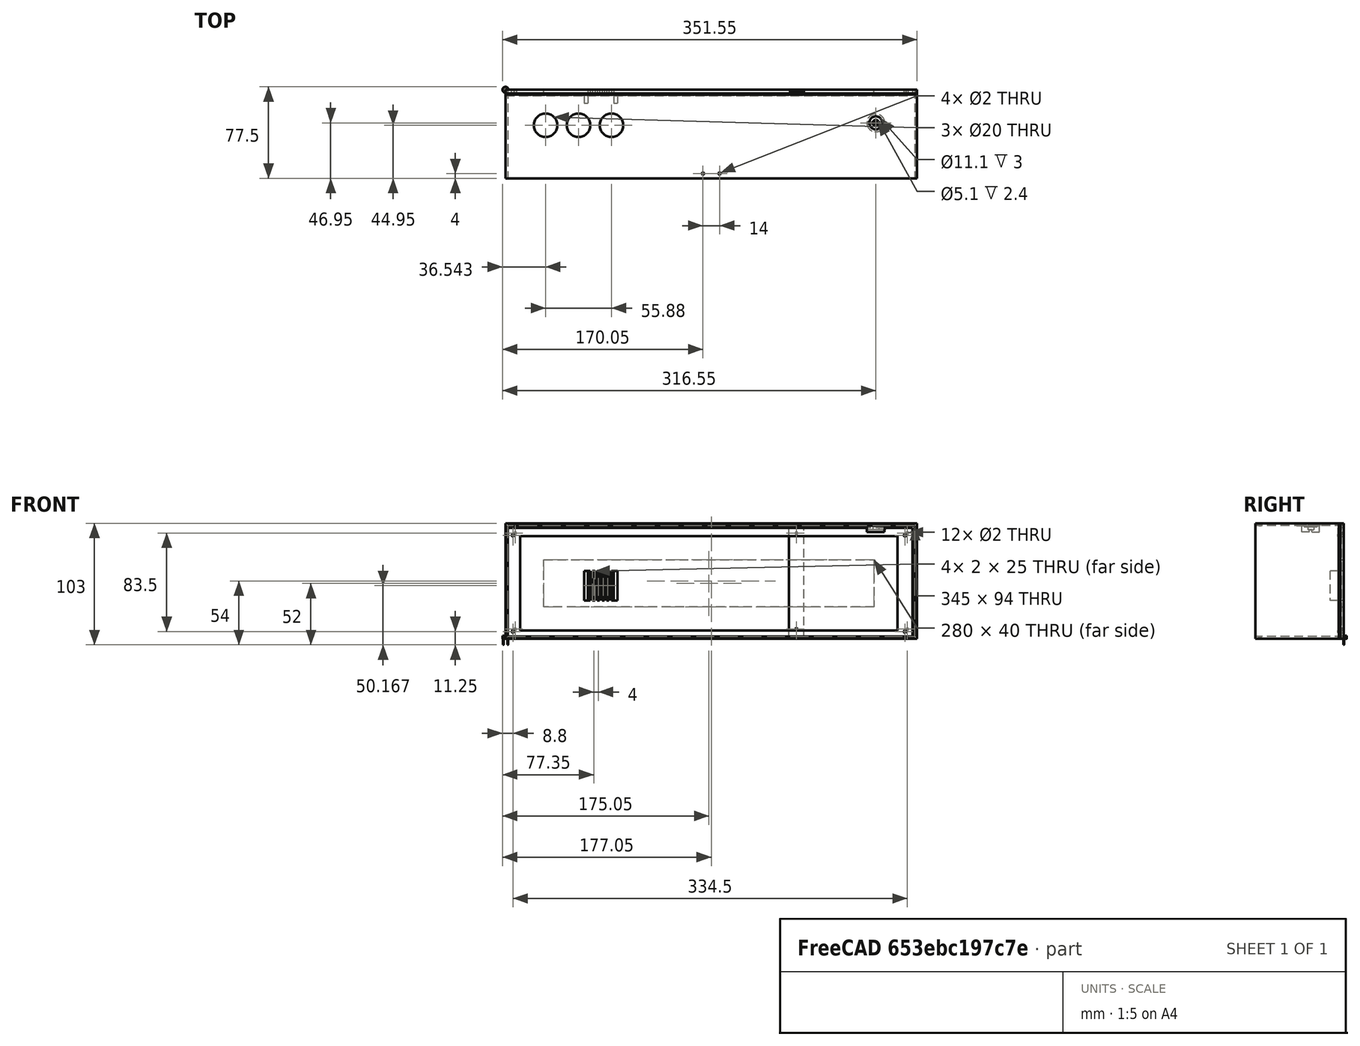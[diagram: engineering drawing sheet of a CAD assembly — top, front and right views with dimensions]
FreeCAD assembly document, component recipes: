
FREECAD ASSEMBLY — COMPONENT RECIPES ("display")

This assembly document has 32 components, labeled P0..P31 below (a component is one placed body or linked part). 31 of them carry a construction recipe — the FreeCAD feature program that regenerates the part from scratch, quoted from this document or its linked companion documents; the rest are supplied as boundary geometry only. No exploded tour is included for this assembly.
COMPONENT P0 — recipe-attached ("BackPlateBody001", modeled in this document).
Construction recipe (the document's own serialized feature program — sketch geometry with constraints, then the solid features built on it; lengths are millimeters unless a unit is written):

FEATURE [Sketcher::SketchObject] Sketch022
  ArcFitTolerance = 1e-06
  AttachmentSupport = -> [XZ_Plane007]
  FullyConstrained = true
  MakeInternals = false
  MapMode = 5
  Placement = pos=(0,0,0) rot=(1,0,0;1.5708rad)
  expr: Constraints[10] = <<CalculatedSS>>.back_plate_width
  expr: Constraints[91] = <<CalculatedSS>>.dht_vertical_offset
  expr: Constraints[92] = <<CalculatedSS>>.dht_horizontal_offset
  expr: Constraints[93] = <<DisplaySS>>.case_thickness + mount_bracket#<<DisplaySS>>.mount_bracket_face_size / 2
  expr: Constraints[94] = <<CalculatedSS>>.split_offset - <<CalculatedSS>>.mount_bracket_face_size / 2
  expr: Constraints[95] = <<DisplaySS>>.screw_diameter
  expr: Constraints[96] = <<CalculatedSS>>.split_offset - <<CalculatedSS>>.mount_bracket_face_size / 2
  expr: Constraints[97] = <<CalculatedSS>>.case_height - <<DisplaySS>>.case_thickness - <<mount_bracket>>#<<DisplaySS>>.mount_bracket_face_size / 2
  expr: Constraints[98] = <<DisplaySS>>.screw_diameter
  expr: Constraints[9] = <<CalculatedSS>>.back_plate_height
  sketch-geometry (35):
    g0: LineSegment StartX=0 StartY=98 StartZ=0 EndX=0 EndY=0 EndZ=0
    g1: LineSegment StartX=0 StartY=0 StartZ=0 EndX=349 EndY=0 EndZ=0
    g2: LineSegment StartX=349 StartY=0 StartZ=0 EndX=349 EndY=98 EndZ=0
    g3: LineSegment StartX=349 StartY=98 StartZ=0 EndX=0 EndY=98 EndZ=0
    g4: LineSegment StartX=69.8 StartY=57.6667 StartZ=0 EndX=69.8 EndY=32.6667 EndZ=0
    g5: LineSegment StartX=69.8 StartY=32.6667 StartZ=0 EndX=71.8 EndY=32.6667 EndZ=0
    g6: LineSegment StartX=71.8 StartY=32.6667 StartZ=0 EndX=71.8 EndY=57.6667 EndZ=0
    g7: LineSegment StartX=71.8 StartY=57.6667 StartZ=0 EndX=69.8 EndY=57.6667 EndZ=0
    g8: LineSegment StartX=73.8 StartY=57.6667 StartZ=0 EndX=73.8 EndY=32.6667 EndZ=0
    g9: LineSegment StartX=73.8 StartY=32.6667 StartZ=0 EndX=75.8 EndY=32.6667 EndZ=0
    g10: LineSegment StartX=75.8 StartY=32.6667 StartZ=0 EndX=75.8 EndY=57.6667 EndZ=0
    g11: LineSegment StartX=75.8 StartY=57.6667 StartZ=0 EndX=73.8 EndY=57.6667 EndZ=0
    g12: LineSegment StartX=77.8 StartY=57.6667 StartZ=0 EndX=77.8 EndY=32.6667 EndZ=0
    g13: LineSegment StartX=77.8 StartY=32.6667 StartZ=0 EndX=79.8 EndY=32.6667 EndZ=0
    g14: LineSegment StartX=79.8 StartY=32.6667 StartZ=0 EndX=79.8 EndY=57.6667 EndZ=0
    g15: LineSegment StartX=79.8 StartY=57.6667 StartZ=0 EndX=77.8 EndY=57.6667 EndZ=0
    g16: LineSegment StartX=81.8 StartY=57.6667 StartZ=0 EndX=81.8 EndY=32.6667 EndZ=0
    g17: LineSegment StartX=81.8 StartY=32.6667 StartZ=0 EndX=83.8 EndY=32.6667 EndZ=0
    g18: LineSegment StartX=83.8 StartY=32.6667 StartZ=0 EndX=83.8 EndY=57.6667 EndZ=0
    g19: LineSegment StartX=83.8 StartY=57.6667 StartZ=0 EndX=81.8 EndY=57.6667 EndZ=0
    g20: LineSegment StartX=85.8 StartY=57.6667 StartZ=0 EndX=85.8 EndY=32.6667 EndZ=0
    g21: LineSegment StartX=85.8 StartY=32.6667 StartZ=0 EndX=87.8 EndY=32.6667 EndZ=0
    g22: LineSegment StartX=87.8 StartY=32.6667 StartZ=0 EndX=87.8 EndY=57.6667 EndZ=0
    g23: LineSegment StartX=87.8 StartY=57.6667 StartZ=0 EndX=85.8 EndY=57.6667 EndZ=0
    g24: LineSegment StartX=89.8 StartY=57.6667 StartZ=0 EndX=89.8 EndY=32.6667 EndZ=0
    g25: LineSegment StartX=89.8 StartY=32.6667 StartZ=0 EndX=91.8 EndY=32.6667 EndZ=0
    g26: LineSegment StartX=91.8 StartY=32.6667 StartZ=0 EndX=91.8 EndY=57.6667 EndZ=0
    g27: LineSegment StartX=91.8 StartY=57.6667 StartZ=0 EndX=89.8 EndY=57.6667 EndZ=0
    g28: LineSegment [constr] StartX=71.8 StartY=57.6667 StartZ=0 EndX=73.8 EndY=57.6667 EndZ=0
    g29: LineSegment [constr] StartX=75.8 StartY=57.6667 StartZ=0 EndX=77.8 EndY=57.6667 EndZ=0
    g30: LineSegment [constr] StartX=79.8 StartY=57.6667 StartZ=0 EndX=81.8 EndY=57.6667 EndZ=0
    g31: LineSegment [constr] StartX=83.8 StartY=57.6667 StartZ=0 EndX=85.8 EndY=57.6667 EndZ=0
    g32: LineSegment [constr] StartX=87.8 StartY=57.6667 StartZ=0 EndX=89.8 EndY=57.6667 EndZ=0
    g33: Circle CenterX=246.75 CenterY=8.25 CenterZ=0 NormalX=0 NormalY=0 NormalZ=1 AngleXU=0 Radius=1
    g34: Circle CenterX=246.75 CenterY=89.75 CenterZ=0 NormalX=0 NormalY=0 NormalZ=1 AngleXU=0 Radius=1
  constraints (99):
    c: Coincident(g0,g1)
    c: Coincident(g1,g2)
    c: Coincident(g2,g3)
    c: Coincident(g3,g0)
    c: Vertical(g0)
    c: Vertical(g2)
    c: Horizontal(g1)
    c: Horizontal(g3)
    c: Coincident(g0,g-1)
    c: Distance(g0) = 98
    c: Distance(g1) = 349
    c: Coincident(g4,g5)
    c: Coincident(g5,g6)
    c: Coincident(g6,g7)
    c: Coincident(g7,g4)
    c: Vertical(g4)
    c: Vertical(g6)
    c: Horizontal(g5)
    c: Horizontal(g7)
    c: Distance(g6) = 25
    c: Distance(g7) = 2
    c: Coincident(g8,g9)
    c: Coincident(g12,g13)
    c: Coincident(g16,g17)
    c: Coincident(g20,g21)
    c: Coincident(g24,g25)
    c: Coincident(g9,g10)
    c: Coincident(g13,g14)
    c: Coincident(g17,g18)
    c: Coincident(g21,g22)
    c: Coincident(g25,g26)
    c: Coincident(g10,g11)
    c: Coincident(g14,g15)
    c: Coincident(g18,g19)
    c: Coincident(g22,g23)
    c: Coincident(g26,g27)
    c: Coincident(g11,g8)
    c: Coincident(g15,g12)
    c: Coincident(g19,g16)
    c: Coincident(g23,g20)
    c: Coincident(g27,g24)
    c: Vertical(g8)
    c: Vertical(g12)
    c: Vertical(g16)
    c: Vertical(g20)
    c: Vertical(g24)
    c: Vertical(g10)
    c: Vertical(g14)
    c: Vertical(g18)
    c: Vertical(g22)
    c: Vertical(g26)
    c: Horizontal(g9)
    c: Horizontal(g13)
    c: Horizontal(g17)
    c: Horizontal(g21)
    c: Horizontal(g25)
    c: Horizontal(g11)
    c: Horizontal(g15)
    c: Horizontal(g19)
    c: Horizontal(g23)
    c: Horizontal(g27)
    c: Coincident(g28,g6)
    c: Coincident(g28,g8)
    c: Horizontal(g28)
    c: Coincident(g29,g10)
    c: Coincident(g29,g12)
    c: Horizontal(g29)
    c: Coincident(g30,g14)
    c: Coincident(g30,g16)
    c: Horizontal(g30)
    c: Coincident(g31,g18)
    c: Coincident(g31,g20)
    c: Horizontal(g31)
    c: Coincident(g32,g22)
    c: Coincident(g32,g24)
    c: Horizontal(g32)
    c: DistanceX(g6,g8) = 2
    c: Equal(g11,g7)
    c: Equal(g7,g15)
    c: Equal(g15,g19)
    c: Equal(g19,g23)
    c: Equal(g23,g27)
    c: Equal(g29,g28)
    c: Equal(g28,g30)
    c: Equal(g30,g31)
    c: Equal(g31,g32)
    c: Horizontal(g4,g8)
    c: Horizontal(g8,g12)
    c: Horizontal(g12,g16)
    c: Horizontal(g16,g20)
    c: Horizontal(g20,g24)
    c: DistanceY(g-1,g4) = 32.6667
    c: DistanceX(g-1,g4) = 69.8
    c: DistanceY(g-1,g33) = 8.25
    c: DistanceX(g-2,g33) = 246.75
    c: Diameter(g33) = 2
    c: DistanceX(g-2,g34) = 246.75
    c: DistanceY(g-1,g34) = 89.75
    c: Diameter(g34) = 2
FEATURE [PartDesign::Pad] Pad007  label="BackPlatePad"
  Direction = (0,-1,2e-16)
  Length = 4
  Length2 = 10
  Placement = pos=(0,0,0) rot=(1,0,0;1.5708rad)
  Profile = -> Sketch022
  ReferenceAxis = -> Sketch022 [N_Axis]
  Refine = true
  Suppressed = false
  Type = 0
  expr: Length = <<DisplaySS>>.back_plate_thickness
FEATURE [Sketcher::SketchObject] Sketch023
  ArcFitTolerance = 1e-06
  AttachmentSupport = -> [XZ_Plane007]
  FullyConstrained = true
  MakeInternals = false
  MapMode = 5
  Placement = pos=(0,0,0) rot=(1,0,0;1.5708rad)
  expr: Constraints[0] = <<CalculatedSS>>.backplate_screw_offset_x
  expr: Constraints[1] = <<CalculatedSS>>.backplate_screw_offset_y
  expr: Constraints[2] = <<DisplaySS>>.screw_diameter
  sketch-geometry (1):
    g0: Circle CenterX=8.25 CenterY=8.25 CenterZ=0 NormalX=0 NormalY=0 NormalZ=1 AngleXU=0 Radius=1
  constraints (3):
    c: DistanceX(g-2,g0) = 8.25
    c: DistanceY(g-1,g0) = 8.25
    c: Diameter(g0) = 2
FEATURE [PartDesign::Plane] DatumPlane012
  AttachmentOffset = pos=(0,0,174.5) rot=(0,0,1;0rad)
  AttachmentSupport = -> [Pad007]
  Length = 138.684
  MapMode = 4
  Placement = pos=(174.5,0,-3.87e-14) rot=(0.707107,0,0.707107;3.14159rad)
  ResizeMode = 0
  Width = 65.6844
  expr: .AttachmentOffset.Base.z = <<CalculatedSS>>.back_plate_width / 2
FEATURE [PartDesign::Plane] DatumPlane013
  AttachmentOffset = pos=(0,0,-49) rot=(0,0,1;0rad)
  AttachmentSupport = -> [Pad007]
  Length = 401.35
  MapMode = 3
  Placement = pos=(0,0,49) rot=(1,0,0;3.14159rad)
  ResizeMode = 0
  Width = 77.3496
  expr: .AttachmentOffset.Base.z = <<CalculatedSS>>.back_plate_height / 2 * -1
FEATURE [Sketcher::SketchObject] Sketch026
  ArcFitTolerance = 1e-06
  AttachmentSupport = -> [XZ_Plane007]
  ExternalGeometry = -> [Sketch022]
  FullyConstrained = true
  MakeInternals = false
  MapMode = 5
  Placement = pos=(0,0,0) rot=(1,0,0;1.5708rad)
  sketch-geometry (8):
    g0: LineSegment StartX=69.8 StartY=57.6667 StartZ=0 EndX=66.8 EndY=57.6667 EndZ=0
    g1: LineSegment StartX=66.8 StartY=57.6667 StartZ=0 EndX=66.8 EndY=32.6667 EndZ=0
    g2: LineSegment StartX=66.8 StartY=32.6667 StartZ=0 EndX=69.8 EndY=32.6667 EndZ=0
    g3: LineSegment StartX=69.8 StartY=32.6667 StartZ=0 EndX=69.8 EndY=57.6667 EndZ=0
    g4: LineSegment StartX=91.8 StartY=57.6667 StartZ=0 EndX=91.8 EndY=32.6667 EndZ=0
    g5: LineSegment StartX=91.8 StartY=32.6667 StartZ=0 EndX=94.8 EndY=32.6667 EndZ=0
    g6: LineSegment StartX=94.8 StartY=32.6667 StartZ=0 EndX=94.8 EndY=57.6667 EndZ=0
    g7: LineSegment StartX=94.8 StartY=57.6667 StartZ=0 EndX=91.8 EndY=57.6667 EndZ=0
  constraints (20):
    c: Coincident(g0,g1)
    c: Coincident(g1,g2)
    c: Coincident(g2,g3)
    c: Coincident(g3,g0)
    c: Horizontal(g0)
    c: Horizontal(g2)
    c: Vertical(g1)
    c: Coincident(g0,g-6)
    c: Coincident(g4,g5)
    c: Coincident(g5,g6)
    c: Coincident(g6,g7)
    c: Coincident(g7,g4)
    c: Vertical(g6)
    c: Horizontal(g5)
    c: Horizontal(g7)
    c: Coincident(g4,g-3)
    c: Coincident(g4,g-4)
    c: Coincident(g2,g-5)
    c: Distance(g2) = 3
    c: Equal(g2,g5)
FEATURE [PartDesign::Pad] Pad008
  BaseFeature = -> Pad007
  Direction = (0,-1,2e-16)
  Length = 11.7
  Length2 = 10
  Placement = pos=(0,0,0) rot=(1,0,0;1.5708rad)
  Profile = -> Sketch026
  ReferenceAxis = -> Sketch026 [N_Axis]
  Refine = true
  Suppressed = false
  Type = 0
  expr: Length = <<DisplaySS>>.back_plate_thickness + <<DisplaySS>>.dht_depth
FEATURE [PartDesign::Plane] DatumPlane015  label="BackPlateFace"
  AttachmentOffset = pos=(0,0,4) rot=(0,0,1;0rad)
  AttachmentSupport = -> [Pad008]
  Length = 416.896
  MapMode = 2
  Placement = pos=(0,-4,9e-16) rot=(1,0,0;1.5708rad)
  ResizeMode = 0
  Width = 165.896
  expr: .AttachmentOffset.Base.z = <<DisplaySS>>.back_plate_thickness
FEATURE [Sketcher::SketchObject] Sketch027  label="MountStudSketch"
  ArcFitTolerance = 1e-06
  AttachmentSupport = -> [DatumPlane015]
  ExternalGeometry = -> [Sketch026]
  FullyConstrained = true
  MakeInternals = false
  MapMode = 5
  Placement = pos=(0,-4,9e-16) rot=(1,0,0;1.5708rad)
  expr: Constraints[0] = <<mount_stud>>#<<MountStudSS>>.base_diameter
  expr: Constraints[6] = mount_stud#<<MountStudSS>>.base_diameter / 2
  sketch-geometry (4):
    g0: Circle CenterX=80.8 CenterY=23.3932 CenterZ=0 NormalX=0 NormalY=0 NormalZ=1 AngleXU=0 Radius=9.2735
    g1: LineSegment [constr] StartX=80.8 StartY=23.3932 StartZ=0 EndX=66.8 EndY=32.6667 EndZ=0
    g2: LineSegment [constr] StartX=80.8 StartY=23.3932 StartZ=0 EndX=94.8 EndY=32.6667 EndZ=0
    g3: LineSegment StartX=80.8 StartY=23.3932 StartZ=0 EndX=80.8 EndY=32.6667 EndZ=0
  constraints (10):
    c: Diameter(g0) = 18.547
    c: Coincident(g1,g0)
    c: Coincident(g1,g-3)
    c: Coincident(g2,g0)
    c: Coincident(g2,g-4)
    c: Equal(g2,g1)
    c: DistanceY(g0,g1) = 9.2735
    c: Coincident(g3,g0)
    c: PointOnObject(g3,g0)
    c: Vertical(g3)
FEATURE [PartDesign::Mirrored] Mirrored
  MirrorPlane = -> DatumPlane013
  Placement = pos=(0,0,0) rot=(1,0,0;1.5708rad)
  Refine = true
  Suppressed = false
  TransformMode = 0
FEATURE [PartDesign::Mirrored] Mirrored006
  MirrorPlane = -> DatumPlane012
  Placement = pos=(0,0,0) rot=(1,0,0;1.5708rad)
  Refine = true
  Suppressed = false
  TransformMode = 0
FEATURE [PartDesign::Pocket] Pocket014
  BaseFeature = -> Pad008
  Direction = (0,1,-2e-16)
  Length = 4
  Length2 = 5
  Placement = pos=(0,0,0) rot=(1,0,0;1.5708rad)
  Profile = -> Sketch023
  ReferenceAxis = -> Sketch023 [N_Axis]
  Refine = true
  Reversed = true
  Suppressed = false
  Type = 0
  expr: Length = <<DisplaySS>>.back_plate_thickness
FEATURE [PartDesign::MultiTransform] MultiTransform
  BaseFeature = -> Pocket014
  Originals = -> [Pocket014]
  Placement = pos=(0,0,0) rot=(1,0,0;1.5708rad)
  Refine = true
  Suppressed = false
  TransformMode = 0
  Transformations = -> [Mirrored,Mirrored006]
FEATURE [PartDesign::Plane] DatumPlane017
  AttachmentOffset = pos=(0,0,2) rot=(0,0,1;0rad)
  AttachmentSupport = -> [XY_Plane007]
  Length = 416.896
  MapMode = 3
  Placement = pos=(0,-2,4e-16) rot=(1,0,0;1.5708rad)
  ResizeMode = 0
  Width = 165.896
  expr: .AttachmentOffset.Base.z = <<DisplaySS>>.back_plate_thickness / 2
FEATURE [Sketcher::SketchObject] Sketch039  label="CutSketch"
  ArcFitTolerance = 1e-06
  AttachmentSupport = -> [XY_Plane007]
  FullyConstrained = true
  MakeInternals = false
  MapMode = 5
  expr: Constraints[19] = <<DisplaySS>>.back_plate_thickness / 2
  expr: Constraints[20] = <<CalculatedSS>>.mount_bracket_face_size
  expr: Constraints[30] = <<DisplaySS>>.back_plate_thickness / 2
  expr: Constraints[41] = <<CalculatedSS>>.split_offset
  expr: Constraints[42] = <<CalculatedSS>>.case_width
  expr: Constraints[9] = <<DisplaySS>>.back_plate_thickness + <<DisplaySS>>.dht_depth
  sketch-geometry (16):
    g0: LineSegment StartX=0 StartY=0 StartZ=0 EndX=0 EndY=-11.7 EndZ=0
    g1: LineSegment StartX=0 StartY=-11.7 StartZ=0 EndX=240.5 EndY=-11.7 EndZ=0
    g2: LineSegment StartX=240.5 StartY=-11.7 StartZ=0 EndX=240.5 EndY=0 EndZ=0
    g3: LineSegment StartX=240.5 StartY=0 StartZ=0 EndX=0 EndY=0 EndZ=0
    g4: LineSegment StartX=240.5 StartY=0 StartZ=0 EndX=240.5 EndY=-2 EndZ=0
    g5: LineSegment StartX=240.5 StartY=-2 StartZ=0 EndX=253 EndY=-2 EndZ=0
    g6: LineSegment StartX=253 StartY=-2 StartZ=0 EndX=253 EndY=0 EndZ=0
    g7: LineSegment StartX=253 StartY=0 StartZ=0 EndX=240.5 EndY=0 EndZ=0
    g8: LineSegment StartX=240.5 StartY=-2 StartZ=0 EndX=240.5 EndY=-4 EndZ=0
    g9: LineSegment StartX=240.5 StartY=-4 StartZ=0 EndX=253 EndY=-4 EndZ=0
    g10: LineSegment StartX=253 StartY=-4 StartZ=0 EndX=253 EndY=-2 EndZ=0
    g11: LineSegment StartX=253 StartY=-2 StartZ=0 EndX=240.5 EndY=-2 EndZ=0
    g12: LineSegment StartX=253 StartY=-4 StartZ=0 EndX=349 EndY=-4 EndZ=0
    g13: LineSegment StartX=349 StartY=-4 StartZ=0 EndX=349 EndY=0 EndZ=0
    g14: LineSegment StartX=349 StartY=0 StartZ=0 EndX=253 EndY=0 EndZ=0
    g15: LineSegment StartX=253 StartY=0 StartZ=0 EndX=253 EndY=-4 EndZ=0
  constraints (43):
    c: Coincident(g0,g1)
    c: Coincident(g1,g2)
    c: Coincident(g2,g3)
    c: Coincident(g3,g0)
    c: Vertical(g0)
    c: Vertical(g2)
    c: Horizontal(g1)
    c: Horizontal(g3)
    c: Coincident(g0,g-1)
    c: Distance(g0) = 11.7
    c: Coincident(g4,g5)
    c: Coincident(g5,g6)
    c: Coincident(g6,g7)
    c: Coincident(g7,g4)
    c: Vertical(g4)
    c: Vertical(g6)
    c: Horizontal(g5)
    c: Horizontal(g7)
    c: Coincident(g4,g2)
    c: Distance(g6) = 2
    c: Distance(g5) = 12.5
    c: Coincident(g8,g9)
    c: Coincident(g9,g10)
    c: Coincident(g10,g11)
    c: Coincident(g11,g8)
    c: Vertical(g8)
    c: Vertical(g10)
    c: Horizontal(g9)
    c: Coincident(g8,g4)
    c: Coincident(g10,g5)
    c: Distance(g10) = 2
    c: Coincident(g12,g13)
    c: Coincident(g13,g14)
    c: Coincident(g14,g15)
    c: Coincident(g15,g12)
    c: Horizontal(g12)
    c: Horizontal(g14)
    c: Vertical(g13)
    c: Vertical(g15)
    c: Coincident(g12,g9)
    c: PointOnObject(g13,g-1)
    c: DistanceX(g-1,g6) = 253
    c: DistanceX(g-2,g13) = 349
FEATURE [PartDesign::Body] Body006  label="FullBackPlateBody"
  AllowCompound = false
  Group = -> [Sketch022,Pad007,Sketch023,DatumPlane012,DatumPlane013,Mirrored,Mirrored006,Sketch026,Pad008,DatumPlane015,Sketch027,Pocket014,MultiTransform,DatumPlane017,Sketch039]
  Origin = -> Origin007
  Tip = -> MultiTransform
COMPONENT P1 — same part as P0; its construction recipe is shown at P0.
COMPONENT P2 — same part as P0; its construction recipe is shown at P0.
COMPONENT P3 — same part as P0; its construction recipe is shown at P0.
COMPONENT P4 — recipe-attached ("Grid", a linked part whose construction recipe lives in a companion FreeCAD document of the same project; that document's serialized recipe follows).
Construction recipe (the companion document, serialized — sketch geometry with constraints, then the solid features built on it; lengths are millimeters unless a unit is written):

FCSTD DOCUMENT  (FreeCAD 1.0R39109 (Git))
Label: grid
License: All rights reserved
LicenseURL: https://en.wikipedia.org/wiki/All_rights_reserved
objects: Sketcher::SketchObject×7, PartDesign::Mirrored×6, PartDesign::Pocket×6, PartDesign::Plane×4, PartDesign::MultiTransform×4, Spreadsheet::Sheet×2, PartDesign::LinearPattern×2, PartDesign::Pad×1, PartDesign::Body×1
note: 64 computed .brp shape members not serialized (recipe doc carries the construction recipe); baked Part::Feature solids carry a one-line shape summary decoded from their .brp

FEATURE [Spreadsheet::Sheet] Spreadsheet  label="GridDisplaySS"
  Body = 0
  cells = A1='Variant; B1='case_depth; C1='matrix_height; D1='matrix_width; E1='matrix_depth; F1='threaded_insert_depth; G1='threaded_insert_outer_diameter; H1='threaded_insert_safety_zone; I1='case_thickness; J1='grid_border_thickness; K1='grid_depth; L1='grid_intercell_spacing; M1='grid_cell_width; N1='led_x_count; O1='led_y_count; P1='grid_countersink_hole_depth; Q1='magnet_diameter; R1='magnet_height; S1='printer_tolerance_modifier; T1='screw_diameter; U1='mount_panel_exclusion_offset; V1='glass_thickness; W1='top_component_offset; X1='photoresistor_diameter; Y1='photoresistor_truncated_width; Z1='photoresistor_height; AA1='top_component_horizontal_offset; AB1='top_component_spacing; AC1='photoresistor_ledge_size; AD1='back_plate_thickness; A2==hiddenref(.Body.String); B2(case_depth)==.B3; C2(matrix_height)==.C3; D2(matrix_width)==.D3; E2(matrix_depth)==.E3; F2(threaded_insert_depth)==.F3; G2(threaded_insert_outer_diameter)==.G3; H2(threaded_insert_safety_zone)==.H3; I2(case_thickness)==.I3; J2(grid_border_thickness)==.J3; K2(grid_depth)==.K3; L2(grid_intercell_spacing)==.L3; M2(grid_cell_width)==.M3; N2(led_x_count)==.N3; O2(led_y_count)==.O3; P2(grid_countersink_hole_depth)==.P3; Q2(magnet_diameter)==.Q3; R2(magnet_height)==.R3; S2(printer_tolerance_modifier)==.S3; T2(screw_diameter)==.T3; U2(mount_panel_exclusion_offset)==.U3; V2(glass_thickness)==.V3; W2(top_component_offset)==.W3; X2(photoresistor_diameter)==.X3; Y2(photoresistor_truncated_width)==.Y3; Z2(photoresistor_height)==.Z3; AA2(top_component_horizontal_offset)==.AA3; AB2(top_component_spacing)==.AB3; AC2(photoresistor_ledge_size)==.AC3; AD2(back_plate_thickness)==.AD3; A3='A; B3==6 cm; C3==80 mm; D3==320 mm; E3==2 mm; F3==4 mm; G3==5 mm; H3==2 mm; I3==2 mm; J3==3 mm; K3==8 mm; L3==1 mm; M3==9 mm; N3=32; O3=8; P3==3 mm; Q3==5 mm; R3==2.8 mm; S3==1 mm; T3==2 mm; U3==2 cm; V3==3 mm; W3==2 cm; X3==5.1 mm; Y3==4.5 mm; Z3==2.4 mm; AA3==2 cm; AB3==0.5 cm; AC3==3 mm; AD3==4 mm
  expr: .Body.Enum = cells[<<A3:|>>]
  expr: .cells.Bind.B2.ZZ2 = tuple(.cells; <<B>> + str(hiddenref(Body) + 3); <<ZZ>> + str(hiddenref(Body) + 3))
FEATURE [Spreadsheet::Sheet] Spreadsheet001  label="GridCalculatedSS"
  cells = B1='grid_horizontal_padding; C1='grid_vertical_padding; D1='case_height; E1='case_width; F1='grid_width; G1='grid_height; H1='grid_matrix_width; I1='grid_matrix_height; J1='screw_horizontal_offset; K1='screw_vertical_offset; L1='grid_magnet_vertical_offset; M1='grid_magnet_horizontal_offset; N1='grid_magnet_depth; O1='case_clear_opening_height; P1='case_clear_opening_width; Q1='mounting_plate_thickness; R1='mount_bracket_face_size; S1='case_relative_magnet_horizontal_offset; T1='case_relative_magnet_vertical_offset; U1='split_offset; V1='screw_offset; W1='screw_diameter; X1='screw_depth; B2(grid_horizontal_padding)==<<GridDisplaySS>>.threaded_insert_outer_diameter + <<GridDisplaySS>>.threaded_insert_safety_zone * 2 + <<GridDisplaySS>>.grid_border_thickness + <<GridDisplaySS>>.grid_intercell_spacing / 2; C2(grid_vertical_padding)==screw_depth + 2 mm; D2(case_height)==grid_height + <<GridDisplaySS>>.case_thickness * 2; E2(case_width)==grid_width + <<GridDisplaySS>>.case_thickness * 2; F2(grid_width)==grid_horizontal_padding * 2 + <<GridDisplaySS>>.matrix_width; G2(grid_height)==grid_vertical_padding * 2 + <<GridDisplaySS>>.matrix_height; H2(grid_matrix_width)==grid_width - 2 * grid_horizontal_padding - 10 mm; I2(grid_matrix_height)=70; J2(screw_horizontal_offset)==grid_horizontal_padding / 2; K2(screw_vertical_offset)==mount_bracket_face_size / 2; L2(grid_magnet_vertical_offset)==grid_height / 5; M2(grid_magnet_horizontal_offset)==grid_horizontal_padding / 2; N2(grid_magnet_depth)==<<GridDisplaySS>>.magnet_height * 2; O2(case_clear_opening_height)==grid_height; P2(case_clear_opening_width)==grid_width; Q2(mounting_plate_thickness)==<<GridDisplaySS>>.matrix_depth + 3 mm; R2(mount_bracket_face_size)==screw_horizontal_offset * 2; S2(case_relative_magnet_horizontal_offset)==grid_magnet_horizontal_offset + <<GridDisplaySS>>.case_thickness; T2(case_relative_magnet_vertical_offset)==grid_magnet_vertical_offset + <<GridDisplaySS>>.case_thickness; U2(split_offset)==grid_width / 2; V2(screw_offset)==screw_diameter + 3 mm; W2(screw_diameter)==4 mm; X2(screw_depth)==5 mm
FEATURE [PartDesign::Plane] DatumPlane003  label="Horizontal Dividing Plane"
  AttachmentOffset = pos=(0,0,-47) rot=(0,0,1;0rad)
  AttachmentSupport = -> [XZ_Plane001]
  Length = 397.203
  MapMode = 3
  Placement = pos=(0,0,47) rot=(1,0,0;3.14159rad)
  ResizeMode = 0
  Width = 77.2029
  expr: .AttachmentOffset.Base.z = <<GridCalculatedSS>>.grid_height / 2 * -1
FEATURE [PartDesign::Mirrored] Mirrored006
  MirrorPlane = -> DatumPlane003
  Placement = pos=(0,0,0) rot=(1,0,0;1.5708rad)
  Refine = true
  Suppressed = false
  TransformMode = 0
FEATURE [PartDesign::Plane] DatumPlane002  label="Vertical Dividing Plane"
  AttachmentOffset = pos=(0,0,172.5) rot=(0,0,1;0rad)
  AttachmentSupport = -> [XZ_Plane001]
  Length = 134.427
  MapMode = 4
  Placement = pos=(172.5,0,-3.83e-14) rot=(0.707107,0,0.707107;3.14159rad)
  ResizeMode = 0
  Width = 65.4272
  expr: .AttachmentOffset.Base.z = <<GridCalculatedSS>>.grid_width / 2
FEATURE [PartDesign::Mirrored] Mirrored007
  MirrorPlane = -> DatumPlane002
  Placement = pos=(0,0,0) rot=(1,0,0;1.5708rad)
  Refine = true
  Suppressed = false
  TransformMode = 0
FEATURE [PartDesign::Plane] DatumPlane001  label="Grid Face Plane"
  AttachmentOffset = pos=(0,0,8) rot=(0,0,1;0rad)
  AttachmentSupport = -> [XZ_Plane001]
  Length = 411.967
  MapMode = 2
  Placement = pos=(0,-8,1.8e-15) rot=(1,0,0;1.5708rad)
  ResizeMode = 0
  Width = 160.967
  expr: .AttachmentOffset.Base.z = <<GridDisplaySS>>.grid_depth
FEATURE [Sketcher::SketchObject] Sketch017  label="ScrewHole"
  ArcFitTolerance = 1e-06
  AttachmentSupport = -> [DatumPlane001]
  FullyConstrained = true
  MakeInternals = false
  MapMode = 5
  Placement = pos=(0,-8,1.8e-15) rot=(1,0,0;1.5708rad)
  expr: Constraints[0] = <<GridDisplaySS>>.screw_diameter
  expr: Constraints[1] = <<GridCalculatedSS>>.screw_horizontal_offset
  expr: Constraints[2] = <<GridCalculatedSS>>.screw_vertical_offset
  sketch-geometry (1):
    g0: Circle CenterX=6.25 CenterY=6.25 CenterZ=0 NormalX=0 NormalY=0 NormalZ=1 AngleXU=0 Radius=1
  constraints (3):
    c: Diameter(g0) = 2
    c: DistanceX(g-2,g0) = 6.25
    c: DistanceY(g-1,g0) = 6.25
FEATURE [PartDesign::Mirrored] Mirrored002
  MirrorPlane = -> DatumPlane003
  Placement = pos=(0,0,0) rot=(1,0,0;1.5708rad)
  Refine = true
  Suppressed = false
  TransformMode = 0
FEATURE [PartDesign::Mirrored] Mirrored003
  MirrorPlane = -> DatumPlane002
  Placement = pos=(0,0,0) rot=(1,0,0;1.5708rad)
  Refine = true
  Suppressed = false
  TransformMode = 0
FEATURE [Sketcher::SketchObject] Sketch005  label="Magnet Hole"
  ArcFitTolerance = 1e-06
  AttachmentSupport = -> [DatumPlane001]
  FullyConstrained = true
  MakeInternals = false
  MapMode = 5
  Placement = pos=(0,-8,1.8e-15) rot=(1,0,0;1.5708rad)
  expr: Constraints[0] = <<GridCalculatedSS>>.grid_magnet_horizontal_offset
  expr: Constraints[1] = <<GridCalculatedSS>>.grid_magnet_vertical_offset
  expr: Constraints[2] = <<GridDisplaySS>>.magnet_diameter
  sketch-geometry (1):
    g0: Circle CenterX=6.25 CenterY=18.8 CenterZ=0 NormalX=0 NormalY=0 NormalZ=1 AngleXU=0 Radius=2.5
  constraints (3):
    c: DistanceX(g-2,g0) = 6.25
    c: DistanceY(g-1,g0) = 18.8
    c: Diameter(g0) = 5
FEATURE [PartDesign::Mirrored] Mirrored
  MirrorPlane = -> DatumPlane003
  Placement = pos=(0,0,0) rot=(1,0,0;1.5708rad)
  Refine = true
  Suppressed = false
  TransformMode = 0
FEATURE [PartDesign::Mirrored] Mirrored001
  MirrorPlane = -> DatumPlane002
  Placement = pos=(0,0,0) rot=(1,0,0;1.5708rad)
  Refine = true
  Suppressed = false
  TransformMode = 0
FEATURE [Sketcher::SketchObject] Sketch004
  ArcFitTolerance = 1e-06
  AttachmentSupport = -> [DatumPlane001]
  FullyConstrained = true
  MakeInternals = false
  MapMode = 5
  Placement = pos=(0,-8,1.8e-15) rot=(1,0,0;1.5708rad)
  expr: Constraints[0] = <<GridCalculatedSS>>.screw_vertical_offset
  expr: Constraints[1] = <<GridCalculatedSS>>.screw_horizontal_offset
  expr: Constraints[2] = <<GridDisplaySS>>.threaded_insert_outer_diameter
  sketch-geometry (1):
    g0: Circle CenterX=6.25 CenterY=6.25 CenterZ=0 NormalX=0 NormalY=0 NormalZ=1 AngleXU=0 Radius=2.5
  constraints (3):
    c: DistanceY(g-1,g0) = 6.25
    c: DistanceX(g-2,g0) = 6.25
    c: Diameter(g0) = 5
FEATURE [Sketcher::SketchObject] Sketch003
  ArcFitTolerance = 1e-06
  AttachmentSupport = -> [DatumPlane001]
  FullyConstrained = true
  MakeInternals = false
  MapMode = 5
  Placement = pos=(0,-8,1.8e-15) rot=(1,0,0;1.5708rad)
  expr: Constraints[10] = <<GridDisplaySS>>.grid_cell_width
  expr: Constraints[11] = <<GridDisplaySS>>.grid_cell_width
  expr: Constraints[8] = <<GridCalculatedSS>>.grid_horizontal_padding
  expr: Constraints[9] = <<GridCalculatedSS>>.grid_vertical_padding
  sketch-geometry (4):
    g0: LineSegment StartX=12.5 StartY=7 StartZ=0 EndX=21.5 EndY=7 EndZ=0
    g1: LineSegment StartX=21.5 StartY=7 StartZ=0 EndX=21.5 EndY=16 EndZ=0
    g2: LineSegment StartX=21.5 StartY=16 StartZ=0 EndX=12.5 EndY=16 EndZ=0
    g3: LineSegment StartX=12.5 StartY=16 StartZ=0 EndX=12.5 EndY=7 EndZ=0
  constraints (12):
    c: Coincident(g0,g1)
    c: Coincident(g1,g2)
    c: Coincident(g2,g3)
    c: Coincident(g3,g0)
    c: Horizontal(g0)
    c: Horizontal(g2)
    c: Vertical(g1)
    c: Vertical(g3)
    c: DistanceX(g-2,g0) = 12.5
    c: DistanceY(g-1,g0) = 7
    c: Distance(g0) = 9
    c: Distance(g1) = 9
FEATURE [PartDesign::LinearPattern] LinearPattern
  Direction = -> Sketch003 [H_Axis]
  Length = 310
  Mode = 0
  Occurrences = 32
  Offset = 10
  Placement = pos=(0,0,0) rot=(1,0,0;1.5708rad)
  Refine = true
  Suppressed = false
  TransformMode = 0
  expr: Length = <<GridCalculatedSS>>.grid_matrix_width
  expr: Occurrences = <<GridDisplaySS>>.led_x_count
FEATURE [PartDesign::LinearPattern] LinearPattern001
  Direction = -> Sketch003 [V_Axis]
  Length = 70
  Mode = 0
  Occurrences = 8
  Offset = 10
  Placement = pos=(0,0,0) rot=(1,0,0;1.5708rad)
  Refine = true
  Suppressed = false
  TransformMode = 0
  expr: Length = <<GridCalculatedSS>>.grid_matrix_height
  expr: Occurrences = <<GridDisplaySS>>.led_y_count
FEATURE [Sketcher::SketchObject] Sketch002
  ArcFitTolerance = 1e-06
  AttachmentSupport = -> [XZ_Plane001]
  FullyConstrained = true
  MakeInternals = false
  MapMode = 5
  Placement = pos=(0,0,0) rot=(1,0,0;1.5708rad)
  expr: Constraints[10] = <<GridCalculatedSS>>.grid_height
  expr: Constraints[9] = <<GridCalculatedSS>>.grid_width
  sketch-geometry (4):
    g0: LineSegment StartX=0 StartY=0 StartZ=0 EndX=345 EndY=0 EndZ=0
    g1: LineSegment StartX=345 StartY=0 StartZ=0 EndX=345 EndY=94 EndZ=0
    g2: LineSegment StartX=345 StartY=94 StartZ=0 EndX=0 EndY=94 EndZ=0
    g3: LineSegment StartX=0 StartY=94 StartZ=0 EndX=0 EndY=0 EndZ=0
  constraints (11):
    c: Coincident(g0,g1)
    c: Coincident(g1,g2)
    c: Coincident(g2,g3)
    c: Coincident(g3,g0)
    c: Horizontal(g0)
    c: Horizontal(g2)
    c: Vertical(g1)
    c: Vertical(g3)
    c: Coincident(g0,g-1)
    c: Distance(g0) = 345
    c: Distance(g3) = 94
FEATURE [PartDesign::Pad] Pad001
  Direction = (0,-1,2e-16)
  Length = 8
  Length2 = 10
  Placement = pos=(0,0,0) rot=(1,0,0;1.5708rad)
  Profile = -> Sketch002
  ReferenceAxis = -> Sketch002 [N_Axis]
  Refine = true
  Suppressed = false
  Type = 0
  expr: Length = <<GridDisplaySS>>.grid_depth
FEATURE [PartDesign::Pocket] Pocket001  label="GridCellPocket"
  BaseFeature = -> Pad001
  Direction = (0,1,-2e-16)
  Length = 8
  Length2 = 5
  Placement = pos=(0,0,0) rot=(1,0,0;1.5708rad)
  Profile = -> Sketch003
  ReferenceAxis = -> Sketch003 [N_Axis]
  Refine = true
  Suppressed = false
  Type = 0
  expr: Length = <<GridDisplaySS>>.grid_depth
FEATURE [PartDesign::MultiTransform] MultiTransform  label="GridCells"
  BaseFeature = -> Pocket001
  Originals = -> [Pocket001]
  Placement = pos=(0,0,0) rot=(1,0,0;1.5708rad)
  Refine = true
  Suppressed = false
  TransformMode = 0
  Transformations = -> [LinearPattern,LinearPattern001]
FEATURE [PartDesign::Pocket] Pocket002  label="ScrewCountersink"
  BaseFeature = -> MultiTransform
  Direction = (0,1,-2e-16)
  Length = 3
  Length2 = 5
  Placement = pos=(0,0,0) rot=(1,0,0;1.5708rad)
  Profile = -> Sketch004
  ReferenceAxis = -> Sketch004 [N_Axis]
  Refine = true
  Suppressed = false
  Type = 0
  expr: Length = <<GridDisplaySS>>.grid_countersink_hole_depth
FEATURE [PartDesign::MultiTransform] MultiTransform001  label="ScrewCountersinks"
  BaseFeature = -> Pocket002
  Originals = -> [Pocket002]
  Placement = pos=(0,0,0) rot=(1,0,0;1.5708rad)
  Refine = true
  Suppressed = false
  TransformMode = 0
  Transformations = -> [Mirrored,Mirrored001]
FEATURE [PartDesign::Pocket] Pocket003  label="Magnet Hole001"
  BaseFeature = -> MultiTransform001
  Direction = (0,1,-2e-16)
  Length = 5.6
  Length2 = 5
  Placement = pos=(0,0,0) rot=(1,0,0;1.5708rad)
  Profile = -> Sketch005
  ReferenceAxis = -> Sketch005 [N_Axis]
  Refine = true
  Suppressed = false
  Type = 0
  expr: Length = <<GridCalculatedSS>>.grid_magnet_depth
FEATURE [PartDesign::MultiTransform] MultiTransform002  label="Magnet Holes"
  BaseFeature = -> Pocket003
  Originals = -> [Pocket003]
  Placement = pos=(0,0,0) rot=(1,0,0;1.5708rad)
  Refine = true
  Suppressed = false
  TransformMode = 0
  Transformations = -> [Mirrored002,Mirrored003]
FEATURE [PartDesign::Pocket] Pocket008  label="ScrewHolePocket"
  BaseFeature = -> MultiTransform002
  Direction = (0,1,-2e-16)
  Length = 5
  Length2 = 5
  Placement = pos=(0,0,0) rot=(1,0,0;1.5708rad)
  Profile = -> Sketch017
  ReferenceAxis = -> Sketch017 [N_Axis]
  Refine = true
  Suppressed = false
  Type = 1
FEATURE [PartDesign::MultiTransform] MultiTransform004  label="GridCellTransform"
  BaseFeature = -> Pocket008
  Originals = -> [Pocket008]
  Placement = pos=(0,0,0) rot=(1,0,0;1.5708rad)
  Refine = true
  Suppressed = false
  TransformMode = 0
  Transformations = -> [Mirrored006,Mirrored007]
FEATURE [Sketcher::SketchObject] Sketch
  ArcFitTolerance = 1e-06
  AttachmentSupport = -> [XY_Plane001]
  FullyConstrained = true
  MakeInternals = false
  MapMode = 5
  expr: Constraints[0] = <<GridCalculatedSS>>.screw_diameter
  expr: Constraints[1] = <<GridCalculatedSS>>.screw_diameter
  expr: Constraints[2] = <<GridCalculatedSS>>.split_offset - <<GridCalculatedSS>>.screw_offset
  expr: Constraints[3] = <<GridCalculatedSS>>.screw_offset * 2
  expr: Constraints[4] = <<GridDisplaySS>>.grid_depth / 2 * -1
  sketch-geometry (2):
    g0: Circle CenterX=165.5 CenterY=-4 CenterZ=0 NormalX=0 NormalY=0 NormalZ=1 AngleXU=0 Radius=2
    g1: Circle CenterX=179.5 CenterY=-4 CenterZ=0 NormalX=0 NormalY=0 NormalZ=1 AngleXU=0 Radius=2
  constraints (6):
    c: Diameter(g1) = 4
    c: Diameter(g0) = 4
    c: DistanceX(g-2,g0) = 165.5
    c: Distance(g0,g1) = 14
    c: DistanceY(g-1,g0) = -4
    c: Horizontal(g0,g1)
FEATURE [PartDesign::Pocket] Pocket
  BaseFeature = -> MultiTransform004
  Direction = (0,0,-1)
  Length = 5
  Length2 = 5
  Placement = pos=(0,0,0) rot=(1,0,0;1.5708rad)
  Profile = -> Sketch
  ReferenceAxis = -> Sketch [N_Axis]
  Refine = true
  Reversed = true
  Suppressed = false
  Type = 0
  expr: Length = <<GridCalculatedSS>>.screw_depth
FEATURE [PartDesign::Plane] DatumPlane  label="GridTopPlane"
  AttachmentOffset = pos=(0,0,94) rot=(0,0,1;0rad)
  AttachmentSupport = -> [XY_Plane001]
  Length = 397.203
  MapMode = 5
  Placement = pos=(0,0,94) rot=(0,0,1;0rad)
  ResizeMode = 0
  Width = 77.2029
  expr: .AttachmentOffset.Base.z = <<GridCalculatedSS>>.grid_height
FEATURE [Sketcher::SketchObject] Sketch018
  ArcFitTolerance = 1e-06
  AttachmentSupport = -> [DatumPlane]
  FullyConstrained = true
  MakeInternals = false
  MapMode = 5
  Placement = pos=(0,0,94) rot=(0,0,1;0rad)
  expr: Constraints[0] = Sketch.Constraints[0]
  expr: Constraints[1] = Sketch.Constraints[1]
  expr: Constraints[2] = Sketch.Constraints[2]
  expr: Constraints[3] = Sketch.Constraints[3]
  expr: Constraints[4] = Sketch.Constraints[4]
  sketch-geometry (2):
    g0: Circle CenterX=165.5 CenterY=-4 CenterZ=0 NormalX=0 NormalY=0 NormalZ=1 AngleXU=0 Radius=2
    g1: Circle CenterX=179.5 CenterY=-4 CenterZ=0 NormalX=0 NormalY=0 NormalZ=1 AngleXU=0 Radius=2
  constraints (6):
    c: Diameter(g1) = 4
    c: Diameter(g0) = 4
    c: DistanceX(g-2,g0) = 165.5
    c: Distance(g0,g1) = 14
    c: DistanceY(g-1,g0) = -4
    c: Horizontal(g0,g1)
FEATURE [PartDesign::Pocket] Pocket009
  BaseFeature = -> Pocket
  Direction = (0,0,-1)
  Length = 5
  Length2 = 5
  Placement = pos=(0,0,0) rot=(1,0,0;1.5708rad)
  Profile = -> Sketch018
  ReferenceAxis = -> Sketch018 [N_Axis]
  Refine = true
  Suppressed = false
  Type = 0
  expr: Length = <<GridCalculatedSS>>.screw_depth
FEATURE [PartDesign::Body] Body001  label="Grid"
  AllowCompound = false
  Group = -> [Sketch002,Pad001,DatumPlane001,Sketch003,Pocket001,MultiTransform,LinearPattern,LinearPattern001,Sketch004,Pocket002,DatumPlane002,DatumPlane003,MultiTransform001,Mirrored,Mirrored001,Sketch005,Pocket003,MultiTransform002,Mirrored002,Mirrored003,Sketch017,Pocket008,MultiTransform004,Mirrored006,Mirrored007,Sketch,Pocket,DatumPlane,Sketch018,Pocket009]
  Origin = -> Origin001
  Tip = -> Pocket009
COMPONENT P5 — recipe-attached ("Housing001", modeled in this document).
Construction recipe (the document's own serialized feature program — sketch geometry with constraints, then the solid features built on it; lengths are millimeters unless a unit is written):

FEATURE [Sketcher::SketchObject] Sketch
  ArcFitTolerance = 1e-06
  AttachmentSupport = -> [XY_Plane]
  FullyConstrained = true
  MakeInternals = false
  MapMode = 3
  Placement = pos=(0,0,0) rot=(1,0,0;1.5708rad)
  expr: Constraints[10] = <<CalculatedSS>>.case_height
  expr: Constraints[9] = <<CalculatedSS>>.case_width
  sketch-geometry (4):
    g0: LineSegment StartX=0 StartY=0 StartZ=0 EndX=349 EndY=0 EndZ=0
    g1: LineSegment StartX=349 StartY=0 StartZ=0 EndX=349 EndY=98 EndZ=0
    g2: LineSegment StartX=349 StartY=98 StartZ=0 EndX=0 EndY=98 EndZ=0
    g3: LineSegment StartX=0 StartY=98 StartZ=0 EndX=0 EndY=0 EndZ=0
  constraints (11):
    c: Coincident(g0,g1)
    c: Coincident(g1,g2)
    c: Coincident(g2,g3)
    c: Coincident(g3,g0)
    c: Horizontal(g0)
    c: Horizontal(g2)
    c: Vertical(g1)
    c: Vertical(g3)
    c: Coincident(g0,g-1)
    c: Distance(g0) = 349
    c: Distance(g3) = 98
FEATURE [Sketcher::SketchObject] Sketch001
  ArcFitTolerance = 1e-06
  AttachmentSupport = -> [XY_Plane]
  FullyConstrained = true
  MakeInternals = false
  MapMode = 3
  Placement = pos=(0,0,0) rot=(1,0,0;1.5708rad)
  expr: Constraints[10] = <<CalculatedSS>>.case_width - <<DisplaySS>>.case_thickness
  expr: Constraints[11] = <<CalculatedSS>>.case_height - <<DisplaySS>>.case_thickness
  expr: Constraints[8] = <<DisplaySS>>.case_thickness
  expr: Constraints[9] = <<DisplaySS>>.case_thickness
  sketch-geometry (4):
    g0: LineSegment StartX=2 StartY=2 StartZ=0 EndX=347 EndY=2 EndZ=0
    g1: LineSegment StartX=347 StartY=2 StartZ=0 EndX=347 EndY=96 EndZ=0
    g2: LineSegment StartX=347 StartY=96 StartZ=0 EndX=2 EndY=96 EndZ=0
    g3: LineSegment StartX=2 StartY=96 StartZ=0 EndX=2 EndY=2 EndZ=0
  constraints (12):
    c: Coincident(g0,g1)
    c: Coincident(g1,g2)
    c: Coincident(g2,g3)
    c: Coincident(g3,g0)
    c: Horizontal(g0)
    c: Horizontal(g2)
    c: Vertical(g1)
    c: Vertical(g3)
    c: DistanceX(g-2,g0) = 2
    c: DistanceY(g-1,g0) = 2
    c: DistanceX(g-2,g1) = 347
    c: DistanceY(g-1,g1) = 96
FEATURE [PartDesign::Pad] Pad
  Direction = (0,-1,2e-16)
  Length = 75
  Length2 = 10
  Profile = -> Sketch
  ReferenceAxis = -> Sketch [N_Axis]
  Refine = true
  Suppressed = false
  Type = 0
  expr: Length = <<DisplaySS>>.case_depth
FEATURE [PartDesign::Pocket] Pocket
  BaseFeature = -> Pad
  Direction = (0,1,-2e-16)
  Length = 5
  Length2 = 5
  Profile = -> Sketch001
  ReferenceAxis = -> Sketch001 [N_Axis]
  Refine = true
  Reversed = true
  Suppressed = false
  Type = 1
FEATURE [PartDesign::Plane] DatumPlane
  AttachmentOffset = pos=(0,0,67) rot=(0,0,1;0rad)
  AttachmentSupport = -> [XZ_Plane]
  Length = 416.896
  MapMode = 2
  Placement = pos=(0,-67,1.49e-14) rot=(1,0,0;1.5708rad)
  ResizeMode = 0
  Width = 165.896
  expr: .AttachmentOffset.Base.z = <<DisplaySS>>.case_depth - <<DisplaySS>>.grid_depth
FEATURE [PartDesign::Plane] DatumPlane007  label="RightInsidePlane"
  AttachmentOffset = pos=(0,0,2) rot=(0,0,1;0rad)
  AttachmentSupport = -> [YZ_Plane]
  Length = 122.181
  MapMode = 5
  Placement = pos=(2,0,0) rot=(0.57735,0.57735,0.57735;2.0944rad)
  ResizeMode = 0
  Width = 145.181
  expr: .AttachmentOffset.Base.z = <<DisplaySS>>.case_thickness
FEATURE [PartDesign::Plane] DatumPlane008  label="LeftInsidePlane"
  AttachmentOffset = pos=(0,0,347) rot=(0,0,1;0rad)
  AttachmentSupport = -> [YZ_Plane]
  Length = 122.181
  MapMode = 5
  Placement = pos=(347,0,0) rot=(0.57735,0.57735,0.57735;2.0944rad)
  ResizeMode = 0
  Width = 145.181
  expr: .AttachmentOffset.Base.z = <<CalculatedSS>>.case_width - <<DisplaySS>>.case_thickness
FEATURE [Sketcher::SketchObject] Sketch015
  ArcFitTolerance = 1e-06
  AttachmentSupport = -> [DatumPlane007]
  FullyConstrained = true
  MakeInternals = false
  MapMode = 5
  Placement = pos=(2,0,0) rot=(0.57735,0.57735,0.57735;2.0944rad)
  expr: Constraints[10] = <<CalculatedSS>>.screw_vertical_offset + <<DisplaySS>>.case_thickness + <<CalculatedSS>>.mount_bracket_face_size / 2
  expr: Constraints[11] = <<CalculatedSS>>.mount_face_offset * -1
  expr: Constraints[20] = <<CalculatedSS>>.mount_face_offset * -1
  expr: Constraints[21] = <<CalculatedSS>>.case_height - <<DisplaySS>>.case_thickness - <<CalculatedSS>>.screw_vertical_offset - <<CalculatedSS>>.mount_bracket_face_size / 2
  expr: Constraints[22] = <<CalculatedSS>>.mount_bracket_face_size
  expr: Constraints[23] = <<CalculatedSS>>.mount_bracket_length
  expr: Constraints[32] = <<CalculatedSS>>.case_height - <<DisplaySS>>.case_thickness
  expr: Constraints[33] = <<CalculatedSS>>.mount_bracket_face_size
  expr: Constraints[34] = <<CalculatedSS>>.mount_bracket_length
  expr: Constraints[43] = <<DisplaySS>>.case_thickness
  expr: Constraints[44] = <<CalculatedSS>>.mount_bracket_face_size
  expr: Constraints[45] = <<CalculatedSS>>.mount_bracket_length
  expr: Constraints[46] = <<DisplaySS>>.back_plate_thickness * -1
  expr: Constraints[47] = <<DisplaySS>>.back_plate_thickness * -1
  expr: Constraints[8] = <<CalculatedSS>>.mount_bracket_length
  expr: Constraints[9] = <<CalculatedSS>>.mount_bracket_face_size
  sketch-geometry (16):
    g0: LineSegment StartX=-62 StartY=2 StartZ=0 EndX=-62 EndY=14.5 EndZ=0
    g1: LineSegment StartX=-62 StartY=14.5 StartZ=0 EndX=-40.1481 EndY=14.5 EndZ=0
    g2: LineSegment StartX=-40.1481 StartY=14.5 StartZ=0 EndX=-40.1481 EndY=2 EndZ=0
    g3: LineSegment StartX=-40.1481 StartY=2 StartZ=0 EndX=-62 EndY=2 EndZ=0
    g4: LineSegment StartX=-62 StartY=83.5 StartZ=0 EndX=-62 EndY=96 EndZ=0
    g5: LineSegment StartX=-62 StartY=96 StartZ=0 EndX=-40.1481 EndY=96 EndZ=0
    g6: LineSegment StartX=-40.1481 StartY=96 StartZ=0 EndX=-40.1481 EndY=83.5 EndZ=0
    g7: LineSegment StartX=-40.1481 StartY=83.5 StartZ=0 EndX=-62 EndY=83.5 EndZ=0
    g8: LineSegment StartX=-25.8519 StartY=96 StartZ=0 EndX=-25.8519 EndY=83.5 EndZ=0
    g9: LineSegment StartX=-25.8519 StartY=83.5 StartZ=0 EndX=-4 EndY=83.5 EndZ=0
    g10: LineSegment StartX=-4 StartY=83.5 StartZ=0 EndX=-4 EndY=96 EndZ=0
    g11: LineSegment StartX=-4 StartY=96 StartZ=0 EndX=-25.8519 EndY=96 EndZ=0
    g12: LineSegment StartX=-25.8519 StartY=14.5 StartZ=0 EndX=-25.8519 EndY=2 EndZ=0
    g13: LineSegment StartX=-25.8519 StartY=2 StartZ=0 EndX=-4 EndY=2 EndZ=0
    g14: LineSegment StartX=-4 StartY=2 StartZ=0 EndX=-4 EndY=14.5 EndZ=0
    g15: LineSegment StartX=-4 StartY=14.5 StartZ=0 EndX=-25.8519 EndY=14.5 EndZ=0
  constraints (48):
    c: Coincident(g0,g1)
    c: Coincident(g1,g2)
    c: Coincident(g2,g3)
    c: Coincident(g3,g0)
    c: Vertical(g0)
    c: Vertical(g2)
    c: Horizontal(g1)
    c: Horizontal(g3)
    c: Distance(g1) = 21.8519
    c: Distance(g2) = 12.5
    c: DistanceY(g-1,g1) = 14.5
    c: DistanceX(g-2,g0) = -62
    c: Coincident(g4,g5)
    c: Coincident(g5,g6)
    c: Coincident(g6,g7)
    c: Coincident(g7,g4)
    c: Vertical(g4)
    c: Vertical(g6)
    c: Horizontal(g5)
    c: Horizontal(g7)
    c: DistanceX(g-2,g4) = -62
    c: DistanceY(g-1,g4) = 83.5
    c: Distance(g4) = 12.5
    c: Distance(g5) = 21.8519
    c: Coincident(g8,g9)
    c: Coincident(g9,g10)
    c: Coincident(g10,g11)
    c: Coincident(g11,g8)
    c: Vertical(g8)
    c: Vertical(g10)
    c: Horizontal(g9)
    c: Horizontal(g11)
    c: DistanceY(g-1,g10) = 96
    c: Distance(g10) = 12.5
    c: Distance(g9) = 21.8519
    c: Coincident(g12,g13)
    c: Coincident(g13,g14)
    c: Coincident(g14,g15)
    c: Coincident(g15,g12)
    c: Vertical(g12)
    c: Vertical(g14)
    c: Horizontal(g13)
    c: Horizontal(g15)
    c: DistanceY(g-1,g13) = 2
    c: Distance(g12) = 12.5
    c: Distance(g15) = 21.8519
    c: DistanceX(g-2,g9) = -4
    c: DistanceX(g-2,g13) = -4
FEATURE [Sketcher::SketchObject] Sketch016
  ArcFitTolerance = 1e-06
  AttachmentSupport = -> [DatumPlane008]
  FullyConstrained = true
  MakeInternals = false
  MapMode = 5
  Placement = pos=(347,0,0) rot=(0.57735,0.57735,0.57735;2.0944rad)
  expr: Constraints[10] = Sketch015.Constraints[10]
  expr: Constraints[11] = Sketch015.Constraints[11]
  expr: Constraints[20] = Sketch015.Constraints[20]
  expr: Constraints[21] = Sketch015.Constraints[21]
  expr: Constraints[22] = Sketch015.Constraints[22]
  expr: Constraints[23] = Sketch015.Constraints[23]
  expr: Constraints[32] = Sketch015.Constraints[32]
  expr: Constraints[33] = Sketch015.Constraints[33]
  expr: Constraints[34] = Sketch015.Constraints[34]
  expr: Constraints[43] = Sketch015.Constraints[43]
  expr: Constraints[44] = Sketch015.Constraints[44]
  expr: Constraints[45] = Sketch015.Constraints[45]
  expr: Constraints[46] = Sketch015.Constraints[46]
  expr: Constraints[47] = Sketch015.Constraints[47]
  expr: Constraints[8] = Sketch015.Constraints[8]
  expr: Constraints[9] = Sketch015.Constraints[9]
  sketch-geometry (16):
    g0: LineSegment StartX=-62 StartY=2 StartZ=0 EndX=-62 EndY=14.5 EndZ=0
    g1: LineSegment StartX=-62 StartY=14.5 StartZ=0 EndX=-40.1481 EndY=14.5 EndZ=0
    g2: LineSegment StartX=-40.1481 StartY=14.5 StartZ=0 EndX=-40.1481 EndY=2 EndZ=0
    g3: LineSegment StartX=-40.1481 StartY=2 StartZ=0 EndX=-62 EndY=2 EndZ=0
    g4: LineSegment StartX=-62 StartY=83.5 StartZ=0 EndX=-62 EndY=96 EndZ=0
    g5: LineSegment StartX=-62 StartY=96 StartZ=0 EndX=-40.1481 EndY=96 EndZ=0
    g6: LineSegment StartX=-40.1481 StartY=96 StartZ=0 EndX=-40.1481 EndY=83.5 EndZ=0
    g7: LineSegment StartX=-40.1481 StartY=83.5 StartZ=0 EndX=-62 EndY=83.5 EndZ=0
    g8: LineSegment StartX=-25.8519 StartY=96 StartZ=0 EndX=-25.8519 EndY=83.5 EndZ=0
    g9: LineSegment StartX=-25.8519 StartY=83.5 StartZ=0 EndX=-4 EndY=83.5 EndZ=0
    g10: LineSegment StartX=-4 StartY=83.5 StartZ=0 EndX=-4 EndY=96 EndZ=0
    g11: LineSegment StartX=-4 StartY=96 StartZ=0 EndX=-25.8519 EndY=96 EndZ=0
    g12: LineSegment StartX=-25.8519 StartY=14.5 StartZ=0 EndX=-25.8519 EndY=2 EndZ=0
    g13: LineSegment StartX=-25.8519 StartY=2 StartZ=0 EndX=-4 EndY=2 EndZ=0
    g14: LineSegment StartX=-4 StartY=2 StartZ=0 EndX=-4 EndY=14.5 EndZ=0
    g15: LineSegment StartX=-4 StartY=14.5 StartZ=0 EndX=-25.8519 EndY=14.5 EndZ=0
  constraints (48):
    c: Coincident(g0,g1)
    c: Coincident(g1,g2)
    c: Coincident(g2,g3)
    c: Coincident(g3,g0)
    c: Vertical(g0)
    c: Vertical(g2)
    c: Horizontal(g1)
    c: Horizontal(g3)
    c: Distance(g1) = 21.8519
    c: Distance(g2) = 12.5
    c: DistanceY(g-1,g1) = 14.5
    c: DistanceX(g-2,g0) = -62
    c: Coincident(g4,g5)
    c: Coincident(g5,g6)
    c: Coincident(g6,g7)
    c: Coincident(g7,g4)
    c: Vertical(g4)
    c: Vertical(g6)
    c: Horizontal(g5)
    c: Horizontal(g7)
    c: DistanceX(g-2,g4) = -62
    c: DistanceY(g-1,g4) = 83.5
    c: Distance(g4) = 12.5
    c: Distance(g5) = 21.8519
    c: Coincident(g8,g9)
    c: Coincident(g9,g10)
    c: Coincident(g10,g11)
    c: Coincident(g11,g8)
    c: Vertical(g8)
    c: Vertical(g10)
    c: Horizontal(g9)
    c: Horizontal(g11)
    c: DistanceY(g-1,g10) = 96
    c: Distance(g10) = 12.5
    c: Distance(g9) = 21.8519
    c: Coincident(g12,g13)
    c: Coincident(g13,g14)
    c: Coincident(g14,g15)
    c: Coincident(g15,g12)
    c: Vertical(g12)
    c: Vertical(g14)
    c: Horizontal(g13)
    c: Horizontal(g15)
    c: DistanceY(g-1,g13) = 2
    c: Distance(g12) = 12.5
    c: Distance(g15) = 21.8519
    c: DistanceX(g-2,g9) = -4
    c: DistanceX(g-2,g13) = -4
FEATURE [PartDesign::Plane] DatumPlane009  label="CaseTopPlane"
  AttachmentOffset = pos=(0,0,98) rot=(0,0,1;0rad)
  AttachmentSupport = -> [XY_Plane]
  Length = 412.678
  MapMode = 5
  Placement = pos=(0,0,98) rot=(0,0,1;0rad)
  ResizeMode = 0
  Width = 138.678
  expr: .AttachmentOffset.Base.z = <<CalculatedSS>>.case_height
FEATURE [PartDesign::Plane] DatumPlane010
  AttachmentOffset = pos=(0,0,28.05) rot=(0,0,1;0rad)
  AttachmentSupport = -> [XZ_Plane]
  Length = 416.896
  MapMode = 5
  Placement = pos=(0,-28.05,6.2e-15) rot=(1,0,0;1.5708rad)
  ResizeMode = 0
  Width = 165.896
  expr: .AttachmentOffset.Base.z = <<DisplaySS>>.top_component_offset
FEATURE [PartDesign::Line] DatumLine
  AttacherType = Attacher::AttachEngineLine
  AttachmentOffset = pos=(-28.05,0,0) rot=(0,0,1;0rad)
  AttachmentSupport = -> [DatumPlane009]
  Length = 20
  MapMode = 16
  Placement = pos=(0,-28.05,98) rot=(0.57735,0.57735,0.57735;2.0944rad)
  ResizeMode = 0
  expr: .AttachmentOffset.Base.x = <<DisplaySS>>.top_component_offset * -1
FEATURE [PartDesign::Plane] DatumPlane011  label="TopComponentPlane"
  AttachmentOffset = pos=(0,0,28.05) rot=(0,0,1;0rad)
  AttachmentSupport = -> [XZ_Plane]
  Length = 416.896
  MapMode = 2
  Placement = pos=(0,-28.05,6.2e-15) rot=(1,0,0;1.5708rad)
  ResizeMode = 0
  Width = 165.896
  expr: .AttachmentOffset.Base.z = <<DisplaySS>>.top_component_offset
FEATURE [PartDesign::Point] DatumPoint
  AttacherType = Attacher::AttachEnginePoint
  AttachmentOffset = pos=(314,98,0) rot=(0,0,1;0rad)
  AttachmentSupport = -> [DatumPlane011]
  MapMode = 32
  Placement = pos=(314,-28.05,98) rot=(1,0,0;1.5708rad)
  expr: .AttachmentOffset.Base.x = <<CalculatedSS>>.case_width - <<DisplaySS>>.top_component_horizontal_offset
  expr: .AttachmentOffset.Base.y = <<CalculatedSS>>.case_height
FEATURE [PartDesign::Line] DatumLine001
  AttacherType = Attacher::AttachEngineLine
  AttachmentSupport = -> [DatumPoint,DatumPlane009]
  Length = 20
  MapMode = 46
  Placement = pos=(314,-28.05,98) rot=(0,0,1;3.14159rad)
  ResizeMode = 0
FEATURE [Sketcher::SketchObject] Sketch019
  ArcFitTolerance = 1e-06
  AttachmentSupport = -> [DatumPlane011]
  ExternalGeometry = -> [DatumPoint]
  FullyConstrained = true
  MakeInternals = false
  MapMode = 5
  Placement = pos=(0,-28.05,6.2e-15) rot=(1,0,0;1.5708rad)
  expr: Constraints[15] = <<DisplaySS>>.photoresistor_diameter / 2
  expr: Constraints[16] = <<DisplaySS>>.photoresistor_ledge_size
  expr: Constraints[17] = <<DisplaySS>>.glass_thickness
  expr: Constraints[18] = <<DisplaySS>>.case_thickness
  expr: Constraints[20] = <<DisplaySS>>.photoresistor_height
  expr: Constraints[21] = <<DisplaySS>>.case_thickness
  sketch-geometry (8):
    g0: LineSegment StartX=319.55 StartY=98 StartZ=0 EndX=319.55 EndY=95 EndZ=0
    g1: LineSegment StartX=319.55 StartY=95 StartZ=0 EndX=316.55 EndY=95 EndZ=0
    g2: LineSegment StartX=316.55 StartY=95 StartZ=0 EndX=316.55 EndY=92.6 EndZ=0
    g3: LineSegment StartX=316.55 StartY=92.6 StartZ=0 EndX=314 EndY=92.6 EndZ=0
    g4: LineSegment StartX=314 StartY=92.6 StartZ=0 EndX=314 EndY=90.6 EndZ=0
    g5: LineSegment StartX=314 StartY=90.6 StartZ=0 EndX=321.55 EndY=90.6 EndZ=0
    g6: LineSegment StartX=321.55 StartY=90.6 StartZ=0 EndX=321.55 EndY=98 EndZ=0
    g7: LineSegment StartX=321.55 StartY=98 StartZ=0 EndX=319.55 EndY=98 EndZ=0
  constraints (24):
    c: Vertical(g0)
    c: Coincident(g0,g1)
    c: Horizontal(g1)
    c: Coincident(g1,g2)
    c: Vertical(g2)
    c: Coincident(g2,g3)
    c: Horizontal(g3)
    c: Coincident(g3,g4)
    c: Vertical(g4)
    c: Coincident(g4,g5)
    c: Horizontal(g5)
    c: Coincident(g5,g6)
    c: Vertical(g6)
    c: Coincident(g6,g7)
    c: Coincident(g7,g0)
    c: Distance(g3) = 2.55
    c: Distance(g1) = 3
    c: Distance(g0) = 3
    c: Distance(g7) = 2
    c: Angle(g7,g6) = 1.5708
    c: Distance(g2) = 2.4
    c: Distance(g4) = 2
    c: DistanceX(g3,g-3) = 0
    c: DistanceY(g0,g-3) = 0
FEATURE [Sketcher::SketchObject] Sketch020
  ArcFitTolerance = 1e-06
  AttachmentSupport = -> [DatumPlane011]
  ExternalGeometry = -> [DatumPoint]
  FullyConstrained = true
  MakeInternals = false
  MapMode = 5
  Placement = pos=(0,-28.05,6.2e-15) rot=(1,0,0;1.5708rad)
  expr: Constraints[15] = Sketch019.Constraints[15]
  expr: Constraints[16] = Sketch019.Constraints[16]
  expr: Constraints[17] = Sketch019.Constraints[17]
  expr: Constraints[18] = Sketch019.Constraints[18]
  expr: Constraints[19] = Sketch019.Constraints[19]
  expr: Constraints[20] = Sketch019.Constraints[20]
  expr: Constraints[21] = Sketch019.Constraints[21]
  expr: Constraints[22] = Sketch019.Constraints[22]
  expr: Constraints[23] = Sketch019.Constraints[23]
  sketch-geometry (8):
    g0: LineSegment StartX=319.55 StartY=98 StartZ=0 EndX=319.55 EndY=95 EndZ=0
    g1: LineSegment StartX=319.55 StartY=95 StartZ=0 EndX=316.55 EndY=95 EndZ=0
    g2: LineSegment StartX=316.55 StartY=95 StartZ=0 EndX=316.55 EndY=92.6 EndZ=0
    g3: LineSegment StartX=316.55 StartY=92.6 StartZ=0 EndX=314 EndY=92.6 EndZ=0
    g4: LineSegment StartX=314 StartY=92.6 StartZ=0 EndX=314 EndY=90.6 EndZ=0
    g5: LineSegment StartX=314 StartY=90.6 StartZ=0 EndX=321.55 EndY=90.6 EndZ=0
    g6: LineSegment StartX=321.55 StartY=90.6 StartZ=0 EndX=321.55 EndY=98 EndZ=0
    g7: LineSegment StartX=321.55 StartY=98 StartZ=0 EndX=319.55 EndY=98 EndZ=0
  constraints (24):
    c: Vertical(g0)
    c: Coincident(g0,g1)
    c: Horizontal(g1)
    c: Coincident(g1,g2)
    c: Vertical(g2)
    c: Coincident(g2,g3)
    c: Horizontal(g3)
    c: Coincident(g3,g4)
    c: Vertical(g4)
    c: Coincident(g4,g5)
    c: Horizontal(g5)
    c: Coincident(g5,g6)
    c: Vertical(g6)
    c: Coincident(g6,g7)
    c: Coincident(g7,g0)
    c: Distance(g3) = 2.55
    c: Distance(g1) = 3
    c: Distance(g0) = 3
    c: Distance(g7) = 2
    c: Angle(g7,g6) = 1.5708
    c: Distance(g2) = 2.4
    c: Distance(g4) = 2
    c: DistanceX(g3,g-3) = 0
    c: DistanceY(g0,g-3) = 0
FEATURE [PartDesign::Groove] Groove
  Angle = 360
  Angle2 = 60
  Axis = (0,0,1)
  Base = (314,-28.05,98)
  BaseFeature = -> Pocket
  Profile = -> Sketch019
  ReferenceAxis = -> DatumLine001
  Refine = true
  Suppressed = false
  Type = 0
FEATURE [PartDesign::Revolution] Revolution
  Angle = 360
  Angle2 = 60
  Axis = (0,0,1)
  Base = (314,-28.05,98)
  BaseFeature = -> Groove
  Profile = -> Sketch020
  ReferenceAxis = -> DatumLine001
  Refine = true
  Suppressed = false
  Type = 0
FEATURE [Sketcher::SketchObject] Sketch021
  ArcFitTolerance = 1e-06
  AttachmentSupport = -> [DatumPlane011]
  ExternalGeometry = -> [DatumPoint]
  FullyConstrained = true
  MakeInternals = false
  MapMode = 5
  Placement = pos=(0,-28.05,6.2e-15) rot=(1,0,0;1.5708rad)
  expr: Constraints[15] = <<DisplaySS>>.glass_thickness + <<DisplaySS>>.photoresistor_height
  expr: Constraints[8] = <<CalculatedSS>>.photoresistor_well_diameter
  expr: Constraints[9] = <<DisplaySS>>.case_thickness
  sketch-geometry (6):
    g0: LineSegment StartX=306.45 StartY=92.6 StartZ=0 EndX=306.45 EndY=90.6 EndZ=0
    g1: LineSegment StartX=306.45 StartY=90.6 StartZ=0 EndX=321.55 EndY=90.6 EndZ=0
    g2: LineSegment StartX=321.55 StartY=90.6 StartZ=0 EndX=321.55 EndY=92.6 EndZ=0
    g3: LineSegment StartX=321.55 StartY=92.6 StartZ=0 EndX=306.45 EndY=92.6 EndZ=0
    g4: LineSegment [constr] StartX=306.45 StartY=92.6 StartZ=0 EndX=314 EndY=98 EndZ=0
    g5: LineSegment [constr] StartX=321.55 StartY=92.6 StartZ=0 EndX=314 EndY=98 EndZ=0
  constraints (16):
    c: Coincident(g0,g1)
    c: Coincident(g1,g2)
    c: Coincident(g2,g3)
    c: Coincident(g3,g0)
    c: Vertical(g0)
    c: Vertical(g2)
    c: Horizontal(g1)
    c: Horizontal(g3)
    c: Distance(g3) = 15.1
    c: Distance(g0) = 2
    c: Coincident(g4,g0)
    c: Coincident(g4,g-3)
    c: Coincident(g5,g2)
    c: Coincident(g5,g4)
    c: Equal(g4,g5)
    c: Distance(g4,g3) = 5.4
FEATURE [PartDesign::Pocket] Pocket010
  BaseFeature = -> Revolution
  Direction = (0,1,-2e-16)
  Length = 1
  Length2 = 1
  Profile = -> Sketch021
  ReferenceAxis = -> Sketch021 [N_Axis]
  Refine = true
  Suppressed = false
  Type = 4
FEATURE [PartDesign::SubShapeBinder] Binder001
  BindCopyOnChange = 0
  BindMode = 0
  ClaimChildren = false
  Context = -> Body [Binder001.]
  Fuse = false
  MakeFace = true
  OffsetFill = false
  OffsetIntersection = false
  OffsetJoinType = 0
  OffsetOpenResult = false
  PartialLoad = false
  Placement = pos=(18.7235,-56.1,98) rot=(0.57735,0.57735,0.57735;2.0944rad)
  Refine = true
  Relative = true
  Support = -> [<external Protoboard.FCStd>#Body007[Sketch020.]]
  _Version = 2
  expr: .Placement.Base.x = <<CalculatedSS>>.mount_bracket_face_size + <<DisplaySS>>.case_thickness + <<CalculatedSS>>.protoboard_long_stud_clearance
  expr: .Placement.Base.y = (<<DisplaySS>>.back_plate_thickness + <<Protoboard>>#<<ProtoboardSS>>.total_width) * -1
  expr: .Placement.Base.z = <<CalculatedSS>>.case_height
FEATURE [Sketcher::SketchObject] Sketch029  label="MountBoardBracketSketch"
  ArcFitTolerance = 1e-06
  AttachmentSupport = -> [DatumPlane009]
  ExternalGeometry = -> [Binder001]
  FullyConstrained = true
  MakeInternals = false
  MapMode = 2
  Placement = pos=(0,0,98) rot=(0,0,1;0rad)
  expr: Constraints[1] = <<Protoboard>>#<<ProtoboardSS>>.mount_hole_diameter / 2
  expr: Constraints[2] = mount_stud#<<MountStudSS>>.base_diameter
  expr: Constraints[4] = <<Protoboard>>#<<ProtoboardSS>>.mount_hole_diameter / 2
  expr: Constraints[6] = <<Protoboard>>#<<ProtoboardSS>>.mount_hole_diameter / 2
  expr: Constraints[7] = <<Protoboard>>#<<ProtoboardSS>>.mount_hole_diameter / 2
  sketch-geometry (4):
    g0: Circle CenterX=186.374 CenterY=-12.25 CenterZ=0 NormalX=0 NormalY=0 NormalZ=1 AngleXU=0 Radius=9.2735
    g1: Circle CenterX=186.374 CenterY=-47.85 CenterZ=0 NormalX=0 NormalY=0 NormalZ=1 AngleXU=0 Radius=9.2735
    g2: Circle CenterX=23.7735 CenterY=-47.85 CenterZ=0 NormalX=0 NormalY=0 NormalZ=1 AngleXU=0 Radius=9.2735
    g3: Circle CenterX=23.7735 CenterY=-12.25 CenterZ=0 NormalX=0 NormalY=0 NormalZ=1 AngleXU=0 Radius=9.2735
  constraints (12):
    c: DistanceX(g-5,g0) = 0
    c: Distance(g0,g-5) = 1.1
    c: Diameter(g0) = 18.547
    c: DistanceX(g1,g-6) = 0
    c: Distance(g1,g-6) = 1.1
    c: Equal(g1,g0)
    c: Distance(g3,g-4) = 1.1
    c: Distance(g2,g-3) = 1.1
    c: DistanceX(g2,g-3) = 0
    c: DistanceX(g3,g-4) = 0
    c: Equal(g3,g2)
    c: Equal(g2,g0)
FEATURE [Sketcher::SketchObject] Sketch024
  ArcFitTolerance = 1e-06
  AttachmentSupport = -> [DatumPlane009]
  ExternalGeometry = -> [DatumPlane011,Sketch029]
  FullyConstrained = true
  MakeInternals = false
  MapMode = 5
  Placement = pos=(0,0,98) rot=(0,0,1;0rad)
  expr: Constraints[0] = <<button>>#<<ButtonSS>>.diameter
  expr: Constraints[6] = <<CalculatedSS>>.button_mount_offset + <<Protoboard>>#<<ProtoboardSS>>.pitch * 3
  sketch-geometry (3):
    g0: Circle CenterX=33.9935 CenterY=-30.05 CenterZ=0 NormalX=0 NormalY=0 NormalZ=1 AngleXU=0 Radius=10
    g1: LineSegment [constr] StartX=33.9935 StartY=-30.05 StartZ=0 EndX=23.7735 EndY=-12.25 EndZ=0
    g2: LineSegment [constr] StartX=33.9935 StartY=-30.05 StartZ=0 EndX=23.7735 EndY=-47.85 EndZ=0
  constraints (7):
    c: Diameter(g0) = 20
    c: Coincident(g1,g0)
    c: Coincident(g1,g-5)
    c: Coincident(g2,g0)
    c: Coincident(g2,g-4)
    c: Equal(g2,g1)
    c: DistanceX(g1,g0) = 10.22
FEATURE [PartDesign::Pocket] Pocket013
  BaseFeature = -> Pocket010
  Direction = (0,0,-1)
  Length = 2
  Length2 = 5
  Profile = -> Sketch024 [Edge1]
  ReferenceAxis = -> Sketch024 [N_Axis]
  Refine = true
  Suppressed = false
  Type = 0
  expr: Length = <<DisplaySS>>.case_thickness
FEATURE [PartDesign::LinearPattern] LinearPattern
  BaseFeature = -> Pocket013
  Direction = -> Sketch024 [H_Axis]
  Length = 55.88
  Mode = 0
  Occurrences = 3
  Offset = 27.94
  Originals = -> [Pocket013]
  Refine = true
  Suppressed = false
  TransformMode = 0
  expr: Length = <<DisplaySS>>.button_diameter * (<<DisplaySS>>.button_count - 1) + <<DisplaySS>>.button_spacing * (<<DisplaySS>>.button_count - 1)
  expr: Occurrences = <<DisplaySS>>.button_count
FEATURE [PartDesign::Plane] DatumPlane014  label="InsideBottomPlane"
  AttachmentOffset = pos=(0,0,2) rot=(0,0,1;0rad)
  AttachmentSupport = -> [LinearPattern]
  Length = 412.678
  MapMode = 2
  Placement = pos=(0,0,2) rot=(0,0,1;0rad)
  ResizeMode = 0
  Width = 138.678
  expr: .AttachmentOffset.Base.z = <<DisplaySS>>.case_thickness
FEATURE [Sketcher::SketchObject] Sketch028  label="InternalPanelAlignmentSketch"
  ArcFitTolerance = 1e-06
  AttachmentSupport = -> [DatumPlane014]
  FullyConstrained = true
  MakeInternals = false
  MapMode = 5
  Placement = pos=(0,0,2) rot=(0,0,1;0rad)
  expr: Constraints[115] = <<CalculatedSS>>.split_offset
  expr: Constraints[17] = <<CalculatedSS>>.case_clear_opening_width
  expr: Constraints[18] = <<DisplaySS>>.case_thickness
  expr: Constraints[19] = <<DisplaySS>>.grid_depth
  expr: Constraints[20] = <<CalculatedSS>>.mounting_plate_thickness
  expr: Constraints[21] = <<DisplaySS>>.case_depth * -1
  expr: Constraints[24] = <<CalculatedSS>>.mount_bracket_length
  expr: Constraints[25] = <<DisplaySS>>.case_thickness
  expr: Constraints[63] = <<CalculatedSS>>.mount_bracket_face_size
  sketch-geometry (42):
    g0: LineSegment StartX=2 StartY=-62 StartZ=0 EndX=2 EndY=-67 EndZ=0
    g1: LineSegment StartX=2 StartY=-67 StartZ=0 EndX=347 EndY=-67 EndZ=0
    g2: LineSegment StartX=347 StartY=-67 StartZ=0 EndX=347 EndY=-62 EndZ=0
    g3: LineSegment StartX=347 StartY=-62 StartZ=0 EndX=2 EndY=-62 EndZ=0
    g4: LineSegment StartX=2 StartY=-67 StartZ=0 EndX=2 EndY=-75 EndZ=0
    g5: LineSegment StartX=2 StartY=-75 StartZ=0 EndX=347 EndY=-75 EndZ=0
    g6: LineSegment StartX=347 StartY=-75 StartZ=0 EndX=347 EndY=-67 EndZ=0
    g7: LineSegment StartX=347 StartY=-67 StartZ=0 EndX=2 EndY=-67 EndZ=0
    g8: LineSegment StartX=2 StartY=0 StartZ=0 EndX=2 EndY=-21.8519 EndZ=0
    g9: LineSegment StartX=2 StartY=-21.8519 StartZ=0 EndX=14.5 EndY=-21.8519 EndZ=0
    g10: LineSegment StartX=14.5 StartY=-21.8519 StartZ=0 EndX=14.5 EndY=0 EndZ=0
    g11: LineSegment StartX=14.5 StartY=0 StartZ=0 EndX=2 EndY=0 EndZ=0
    g12: LineSegment StartX=2 StartY=-62 StartZ=0 EndX=14.5 EndY=-62 EndZ=0
    g13: LineSegment StartX=347 StartY=-62 StartZ=0 EndX=347 EndY=-40.1481 EndZ=0
    g14: LineSegment StartX=347 StartY=-40.1481 StartZ=0 EndX=334.5 EndY=-40.1481 EndZ=0
    g15: LineSegment StartX=334.5 StartY=-40.1481 StartZ=0 EndX=334.5 EndY=-62 EndZ=0
    g16: LineSegment StartX=334.5 StartY=-62 StartZ=0 EndX=347 EndY=-62 EndZ=0
    g17: LineSegment StartX=347 StartY=0 StartZ=0 EndX=334.5 EndY=0 EndZ=0
    g18: LineSegment StartX=334.5 StartY=0 StartZ=0 EndX=334.5 EndY=-21.8519 EndZ=0
    g19: LineSegment StartX=334.5 StartY=-21.8519 StartZ=0 EndX=347 EndY=-21.8519 EndZ=0
    g20: LineSegment StartX=347 StartY=-21.8519 StartZ=0 EndX=347 EndY=0 EndZ=0
    g21: LineSegment [constr] StartX=347 StartY=-75 StartZ=0 EndX=347 EndY=0 EndZ=0
    g22: LineSegment StartX=2 StartY=-62 StartZ=0 EndX=14.5 EndY=-62 EndZ=0
    g23: LineSegment StartX=14.5 StartY=-62 StartZ=0 EndX=14.5 EndY=-40.1481 EndZ=0
    g24: LineSegment StartX=14.5 StartY=-40.1481 StartZ=0 EndX=2 EndY=-40.1481 EndZ=0
    g25: LineSegment StartX=2 StartY=-40.1481 StartZ=0 EndX=2 EndY=-62 EndZ=0
    g26: LineSegment StartX=231.148 StartY=-49.5 StartZ=0 EndX=231.148 EndY=-62 EndZ=0
    g27: LineSegment StartX=231.148 StartY=-62 StartZ=0 EndX=253 EndY=-62 EndZ=0
    g28: LineSegment StartX=253 StartY=-62 StartZ=0 EndX=253 EndY=-49.5 EndZ=0
    g29: LineSegment StartX=253 StartY=-49.5 StartZ=0 EndX=231.148 EndY=-49.5 EndZ=0
    g30: LineSegment StartX=253 StartY=-49.5 StartZ=0 EndX=253 EndY=-62 EndZ=0
    g31: LineSegment StartX=253 StartY=-62 StartZ=0 EndX=274.852 EndY=-62 EndZ=0
    g32: LineSegment StartX=274.852 StartY=-62 StartZ=0 EndX=274.852 EndY=-49.5 EndZ=0
    g33: LineSegment StartX=274.852 StartY=-49.5 StartZ=0 EndX=253 EndY=-49.5 EndZ=0
    g34: LineSegment StartX=253 StartY=0 StartZ=0 EndX=231.148 EndY=0 EndZ=0
    g35: LineSegment StartX=231.148 StartY=0 StartZ=0 EndX=231.148 EndY=-12.5 EndZ=0
    g36: LineSegment StartX=231.148 StartY=-12.5 StartZ=0 EndX=253 EndY=-12.5 EndZ=0
    g37: LineSegment StartX=253 StartY=-12.5 StartZ=0 EndX=253 EndY=0 EndZ=0
    g38: LineSegment StartX=253 StartY=0 StartZ=0 EndX=253 EndY=-12.5 EndZ=0
    g39: LineSegment StartX=253 StartY=-12.5 StartZ=0 EndX=274.852 EndY=-12.5 EndZ=0
    g40: LineSegment StartX=274.852 StartY=-12.5 StartZ=0 EndX=274.852 EndY=0 EndZ=0
    g41: LineSegment StartX=274.852 StartY=0 StartZ=0 EndX=253 EndY=0 EndZ=0
  constraints (118):
    c: Coincident(g0,g1)
    c: Coincident(g1,g2)
    c: Coincident(g2,g3)
    c: Coincident(g3,g0)
    c: Vertical(g0)
    c: Vertical(g2)
    c: Horizontal(g1)
    c: Horizontal(g3)
    c: Coincident(g4,g5)
    c: Coincident(g5,g6)
    c: Coincident(g6,g7)
    c: Coincident(g7,g4)
    c: Vertical(g4)
    c: Vertical(g6)
    c: Horizontal(g5)
    c: Coincident(g4,g0)
    c: Coincident(g6,g1)
    c: Distance(g1) = 345
    c: DistanceX(g-2,g0) = 2
    c: Distance(g4) = 8
    c: Distance(g0) = 5
    c: DistanceY(g-1,g4) = -75
    c: Horizontal(g11)
    c: DistanceY(g-1,g8) = 0
    c: Distance(g10) = 21.8519
    c: DistanceX(g-2,g8) = 2
    c: Horizontal(g12)
    c: Coincident(g13,g14)
    c: Coincident(g14,g15)
    c: Coincident(g15,g16)
    c: Coincident(g16,g13)
    c: Vertical(g13)
    c: Vertical(g15)
    c: Horizontal(g14)
    c: Horizontal(g16)
    c: Coincident(g13,g2)
    c: Coincident(g17,g18)
    c: Coincident(g18,g19)
    c: Coincident(g19,g20)
    c: Coincident(g20,g17)
    c: Horizontal(g17)
    c: Horizontal(g19)
    c: Vertical(g18)
    c: Vertical(g20)
    c: PointOnObject(g17,g-1)
    c: Equal(g18,g15)
    c: Equal(g15,g10)
    c: Equal(g17,g14)
    c: Equal(g14,g11)
    c: Coincident(g21,g5)
    c: Vertical(g21)
    c: Coincident(g21,g17)
    c: Coincident(g22,g23)
    c: Coincident(g23,g24)
    c: Coincident(g24,g25)
    c: Coincident(g25,g22)
    c: Horizontal(g24)
    c: Vertical(g23)
    c: Vertical(g25)
    c: Coincident(g22,g12)
    c: DistanceX(g23,g9) = 0
    c: Equal(g25,g8)
    c: Coincident(g0,g12)
    c: Distance(g9) = 12.5
    c: Coincident(g8,g9)
    c: Coincident(g9,g10)
    c: Angle(g9,g8) = 1.5708
    c: Coincident(g10,g11)
    c: Coincident(g11,g8)
    c: Angle(g11,g10) = 1.5708
    c: Equal(g11,g9)
    c: Coincident(g12,g22)
    c: Coincident(g26,g27)
    c: Coincident(g27,g28)
    c: Coincident(g28,g29)
    c: Coincident(g29,g26)
    c: Vertical(g26)
    c: Vertical(g28)
    c: Horizontal(g27)
    c: Horizontal(g29)
    c: PointOnObject(g27,g3)
    c: Coincident(g30,g31)
    c: Coincident(g31,g32)
    c: Coincident(g32,g33)
    c: Coincident(g33,g30)
    c: Vertical(g30)
    c: Vertical(g32)
    c: Horizontal(g31)
    c: Horizontal(g33)
    c: PointOnObject(g31,g3)
    c: PointOnObject(g34,g-1)
    c: Equal(g32,g24)
    c: Equal(g29,g23)
    c: Equal(g33,g29)
    c: Coincident(g34,g35)
    c: Coincident(g35,g36)
    c: Coincident(g36,g37)
    c: Coincident(g37,g34)
    c: Horizontal(g34)
    c: Horizontal(g36)
    c: Vertical(g35)
    c: Vertical(g37)
    c: Coincident(g38,g39)
    c: Coincident(g39,g40)
    c: Coincident(g40,g41)
    c: Coincident(g41,g38)
    c: Vertical(g38)
    c: Vertical(g40)
    c: Horizontal(g39)
    c: Horizontal(g41)
    c: Vertical(g39,g32)
    c: Vertical(g35,g26)
    c: Equal(g35,g26)
    c: Equal(g40,g32)
    c: Coincident(g28,g30)
    c: DistanceX(g-2,g28) = 253
    c: Coincident(g38,g36)
    c: Equal(g36,g29)
FEATURE [Sketcher::SketchObject] Sketch031  label="Mounting Stud Sketch"
  ArcFitTolerance = 1e-06
  AttachmentSupport = -> [DatumPlane009]
  ExternalGeometry = -> [Binder001]
  FullyConstrained = true
  MakeInternals = false
  MapMode = 5
  Placement = pos=(0,0,98) rot=(0,0,1;0rad)
  expr: Constraints[9] = mount_stud#<<MountStudSS>>.base_diameter / 2
  sketch-geometry (4):
    g0: LineSegment StartX=23.7735 StartY=-12.25 StartZ=0 EndX=33.047 EndY=-12.25 EndZ=0
    g1: LineSegment StartX=23.7735 StartY=-47.85 StartZ=0 EndX=33.047 EndY=-47.85 EndZ=0
    g2: LineSegment StartX=186.374 StartY=-12.25 StartZ=0 EndX=195.647 EndY=-12.25 EndZ=0
    g3: LineSegment StartX=186.374 StartY=-47.85 StartZ=0 EndX=195.647 EndY=-47.85 EndZ=0
  constraints (12):
    c: Coincident(g0,g-7)
    c: Horizontal(g0)
    c: Coincident(g1,g-5)
    c: Coincident(g2,g-3)
    c: Coincident(g3,g-4)
    c: Horizontal(g3)
    c: Equal(g3,g2)
    c: Equal(g2,g1)
    c: Equal(g1,g0)
    c: Distance(g0) = 9.2735
    c: Parallel(g1,g0)
    c: Parallel(g0,g2)
FEATURE [PartDesign::SubShapeBinder] Binder002  label="grid_screw_binder"
  BindCopyOnChange = 0
  BindMode = 0
  ClaimChildren = false
  Context = -> Body [Binder002.]
  Fuse = false
  MakeFace = true
  OffsetFill = false
  OffsetIntersection = false
  OffsetJoinType = 0
  OffsetOpenResult = false
  PartialLoad = false
  Placement = pos=(2,-67,98) rot=(0,0,1;0rad)
  Refine = true
  Relative = true
  Support = -> [<external grid.FCStd>#Body001[Sketch.]]
  _Version = 2
  expr: .Placement.Base.x = <<DisplaySS>>.case_thickness
  expr: .Placement.Base.y = (<<DisplaySS>>.case_depth - <<DisplaySS>>.grid_depth) * -1
  expr: .Placement.Base.z = <<CalculatedSS>>.case_height
FEATURE [Sketcher::SketchObject] Sketch032
  ArcFitTolerance = 1e-06
  AttachmentSupport = -> [DatumPlane009]
  ExternalGeometry = -> [Binder002]
  FullyConstrained = true
  MakeInternals = false
  MapMode = 5
  Placement = pos=(0,0,98) rot=(0,0,1;0rad)
  expr: Constraints[1] = <<DisplaySS>>.screw_diameter
  expr: Constraints[3] = <<DisplaySS>>.screw_diameter
  sketch-geometry (2):
    g0: Circle CenterX=167.5 CenterY=-71 CenterZ=0 NormalX=0 NormalY=0 NormalZ=1 AngleXU=0 Radius=1
    g1: Circle CenterX=181.5 CenterY=-71 CenterZ=0 NormalX=0 NormalY=0 NormalZ=1 AngleXU=0 Radius=1
  constraints (4):
    c: Coincident(g0,g-3)
    c: Diameter(g0) = 2
    c: Coincident(g1,g-4)
    c: Diameter(g1) = 2
FEATURE [PartDesign::Pocket] Pocket015
  BaseFeature = -> LinearPattern
  Direction = (0,0,-1)
  Length = 5
  Length2 = 5
  Profile = -> Sketch032
  ReferenceAxis = -> Sketch032 [N_Axis]
  Refine = true
  Suppressed = false
  Type = 1
FEATURE [Sketcher::SketchObject] Sketch033  label="MountBracketPositionSketch"
  ArcFitTolerance = 1e-06
  AttachmentSupport = -> [DatumPlane014]
  ExternalGeometry = -> [Sketch028]
  FullyConstrained = true
  MakeInternals = false
  MapMode = 5
  Placement = pos=(0,0,2) rot=(0,0,1;0rad)
  expr: Constraints[19] = mount_bracket#<<DisplaySS>>.mount_bracket_length
  expr: Constraints[20] = mount_bracket#<<DisplaySS>>.mount_bracket_face_size
  expr: Constraints[54] = <<CalculatedSS>>.split_offset
  sketch-geometry (36):
    g0: LineSegment [constr] StartX=2 StartY=0 StartZ=0 EndX=2 EndY=-62 EndZ=0
    g1: LineSegment [constr] StartX=2 StartY=-62 StartZ=0 EndX=347 EndY=-62 EndZ=0
    g2: LineSegment [constr] StartX=347 StartY=-62 StartZ=0 EndX=347 EndY=0 EndZ=0
    g3: LineSegment [constr] StartX=347 StartY=0 StartZ=0 EndX=2 EndY=0 EndZ=0
    g4: LineSegment StartX=2 StartY=0 StartZ=0 EndX=2 EndY=-21.8519 EndZ=0
    g5: LineSegment StartX=2 StartY=-21.8519 StartZ=0 EndX=14.5 EndY=-21.8519 EndZ=0
    g6: LineSegment StartX=14.5 StartY=-21.8519 StartZ=0 EndX=14.5 EndY=0 EndZ=0
    g7: LineSegment StartX=14.5 StartY=0 StartZ=0 EndX=2 EndY=0 EndZ=0
    g8: LineSegment StartX=2 StartY=-62 StartZ=0 EndX=14.5 EndY=-62 EndZ=0
    g9: LineSegment StartX=14.5 StartY=-62 StartZ=0 EndX=14.5 EndY=-40.1481 EndZ=0
    g10: LineSegment StartX=14.5 StartY=-40.1481 StartZ=0 EndX=2 EndY=-40.1481 EndZ=0
    g11: LineSegment StartX=2 StartY=-40.1481 StartZ=0 EndX=2 EndY=-62 EndZ=0
    g12: LineSegment StartX=231.148 StartY=-12.5 StartZ=0 EndX=253 EndY=-12.5 EndZ=0
    g13: LineSegment StartX=253 StartY=-12.5 StartZ=0 EndX=253 EndY=0 EndZ=0
    g14: LineSegment StartX=253 StartY=0 StartZ=0 EndX=231.148 EndY=0 EndZ=0
    g15: LineSegment StartX=231.148 StartY=0 StartZ=0 EndX=231.148 EndY=-12.5 EndZ=0
    g16: LineSegment StartX=253 StartY=0 StartZ=0 EndX=253 EndY=-12.5 EndZ=0
    g17: LineSegment StartX=253 StartY=-12.5 StartZ=0 EndX=274.852 EndY=-12.5 EndZ=0
    g18: LineSegment StartX=274.852 StartY=-12.5 StartZ=0 EndX=274.852 EndY=0 EndZ=0
    g19: LineSegment StartX=274.852 StartY=0 StartZ=0 EndX=253 EndY=0 EndZ=0
    g20: LineSegment StartX=231.148 StartY=-62 StartZ=0 EndX=253 EndY=-62 EndZ=0
    g21: LineSegment StartX=253 StartY=-62 StartZ=0 EndX=253 EndY=-49.5 EndZ=0
    g22: LineSegment StartX=253 StartY=-49.5 StartZ=0 EndX=231.148 EndY=-49.5 EndZ=0
    g23: LineSegment StartX=231.148 StartY=-49.5 StartZ=0 EndX=231.148 EndY=-62 EndZ=0
    g24: LineSegment StartX=253 StartY=-49.5 StartZ=0 EndX=253 EndY=-62 EndZ=0
    g25: LineSegment StartX=253 StartY=-62 StartZ=0 EndX=274.852 EndY=-62 EndZ=0
    g26: LineSegment StartX=274.852 StartY=-62 StartZ=0 EndX=274.852 EndY=-49.5 EndZ=0
    g27: LineSegment StartX=274.852 StartY=-49.5 StartZ=0 EndX=253 EndY=-49.5 EndZ=0
    g28: LineSegment StartX=347 StartY=0 StartZ=0 EndX=334.5 EndY=0 EndZ=0
    g29: LineSegment StartX=334.5 StartY=0 StartZ=0 EndX=334.5 EndY=-21.8519 EndZ=0
    g30: LineSegment StartX=334.5 StartY=-21.8519 StartZ=0 EndX=347 EndY=-21.8519 EndZ=0
    g31: LineSegment StartX=347 StartY=-21.8519 StartZ=0 EndX=347 EndY=0 EndZ=0
    g32: LineSegment StartX=347 StartY=-62 StartZ=0 EndX=347 EndY=-40.1481 EndZ=0
    g33: LineSegment StartX=347 StartY=-40.1481 StartZ=0 EndX=334.5 EndY=-40.1481 EndZ=0
    g34: LineSegment StartX=334.5 StartY=-40.1481 StartZ=0 EndX=334.5 EndY=-62 EndZ=0
    g35: LineSegment StartX=334.5 StartY=-62 StartZ=0 EndX=347 EndY=-62 EndZ=0
  constraints (100):
    c: Coincident(g0,g1)
    c: Coincident(g1,g2)
    c: Coincident(g2,g3)
    c: Coincident(g3,g0)
    c: Vertical(g0)
    c: Vertical(g2)
    c: Horizontal(g1)
    c: Horizontal(g3)
    c: Coincident(g0,g-5)
    c: Coincident(g1,g-4)
    c: Coincident(g4,g5)
    c: Coincident(g5,g6)
    c: Coincident(g6,g7)
    c: Coincident(g7,g4)
    c: Vertical(g4)
    c: Vertical(g6)
    c: Horizontal(g5)
    c: Horizontal(g7)
    c: Coincident(g4,g0)
    c: Distance(g6) = 21.8519
    c: Distance(g5) = 12.5
    c: Coincident(g8,g9)
    c: Coincident(g9,g10)
    c: Coincident(g10,g11)
    c: Coincident(g11,g8)
    c: Horizontal(g8)
    c: Horizontal(g10)
    c: Vertical(g9)
    c: Vertical(g11)
    c: Coincident(g8,g0)
    c: Vertical(g9,g5)
    c: Equal(g9,g6)
    c: Coincident(g12,g13)
    c: Coincident(g13,g14)
    c: Coincident(g14,g15)
    c: Coincident(g15,g12)
    c: Horizontal(g12)
    c: Horizontal(g14)
    c: Vertical(g13)
    c: Vertical(g15)
    c: PointOnObject(g13,g3)
    c: Coincident(g16,g17)
    c: Coincident(g17,g18)
    c: Coincident(g18,g19)
    c: Coincident(g19,g16)
    c: Vertical(g16)
    c: Vertical(g18)
    c: Horizontal(g17)
    c: Horizontal(g19)
    c: Coincident(g16,g13)
    c: Equal(g15,g18)
    c: Equal(g18,g5)
    c: Equal(g17,g12)
    c: Equal(g12,g6)
    c: DistanceX(g-1,g13) = 253
    c: Coincident(g20,g21)
    c: Coincident(g21,g22)
    c: Coincident(g22,g23)
    c: Coincident(g23,g20)
    c: Horizontal(g20)
    c: Horizontal(g22)
    c: Vertical(g21)
    c: Vertical(g23)
    c: PointOnObject(g20,g1)
    c: Equal(g23,g15)
    c: Equal(g22,g12)
    c: Coincident(g24,g25)
    c: Coincident(g25,g26)
    c: Coincident(g26,g27)
    c: Coincident(g27,g24)
    c: Vertical(g24)
    c: Vertical(g26)
    c: Horizontal(g25)
    c: Horizontal(g27)
    c: Coincident(g24,g21)
    c: PointOnObject(g25,g1)
    c: Equal(g27,g17)
    c: Vertical(g21,g12)
    c: Coincident(g28,g29)
    c: Coincident(g29,g30)
    c: Coincident(g30,g31)
    c: Coincident(g31,g28)
    c: Horizontal(g28)
    c: Horizontal(g30)
    c: Vertical(g29)
    c: Vertical(g31)
    c: Coincident(g28,g2)
    c: Equal(g29,g17)
    c: Equal(g30,g18)
    c: Coincident(g32,g33)
    c: Coincident(g33,g34)
    c: Coincident(g34,g35)
    c: Coincident(g35,g32)
    c: Vertical(g32)
    c: Vertical(g34)
    c: Horizontal(g33)
    c: Horizontal(g35)
    c: Coincident(g32,g1)
    c: Vertical(g33,g29)
    c: Equal(g34,g29)
FEATURE [PartDesign::Plane] DatumPlane016  label="InternalUpperWallPlane"
  AttachmentOffset = pos=(0,0,96) rot=(0,0,1;0rad)
  AttachmentSupport = -> [XY_Plane]
  Length = 412.678
  MapMode = 5
  Placement = pos=(0,0,96) rot=(0,0,1;0rad)
  ResizeMode = 0
  Width = 138.678
  expr: .AttachmentOffset.Base.z = <<CalculatedSS>>.case_height - <<DisplaySS>>.case_thickness
FEATURE [Sketcher::SketchObject] Sketch034  label="UpperMountBracketPositionSketch"
  ArcFitTolerance = 1e-06
  AttachmentSupport = -> [DatumPlane016]
  ExternalGeometry = -> [Sketch028]
  FullyConstrained = true
  MakeInternals = false
  MapMode = 5
  Placement = pos=(0,0,96) rot=(0,0,1;0rad)
  expr: Constraints[19] = Sketch033.Constraints[19]
  expr: Constraints[20] = Sketch033.Constraints[20]
  expr: Constraints[54] = Sketch033.Constraints[54]
  sketch-geometry (36):
    g0: LineSegment [constr] StartX=2 StartY=0 StartZ=0 EndX=2 EndY=-62 EndZ=0
    g1: LineSegment [constr] StartX=2 StartY=-62 StartZ=0 EndX=347 EndY=-62 EndZ=0
    g2: LineSegment [constr] StartX=347 StartY=-62 StartZ=0 EndX=347 EndY=0 EndZ=0
    g3: LineSegment [constr] StartX=347 StartY=0 StartZ=0 EndX=2 EndY=0 EndZ=0
    g4: LineSegment StartX=2 StartY=0 StartZ=0 EndX=2 EndY=-21.8519 EndZ=0
    g5: LineSegment StartX=2 StartY=-21.8519 StartZ=0 EndX=14.5 EndY=-21.8519 EndZ=0
    g6: LineSegment StartX=14.5 StartY=-21.8519 StartZ=0 EndX=14.5 EndY=0 EndZ=0
    g7: LineSegment StartX=14.5 StartY=0 StartZ=0 EndX=2 EndY=0 EndZ=0
    g8: LineSegment StartX=2 StartY=-62 StartZ=0 EndX=14.5 EndY=-62 EndZ=0
    g9: LineSegment StartX=14.5 StartY=-62 StartZ=0 EndX=14.5 EndY=-40.1481 EndZ=0
    g10: LineSegment StartX=14.5 StartY=-40.1481 StartZ=0 EndX=2 EndY=-40.1481 EndZ=0
    g11: LineSegment StartX=2 StartY=-40.1481 StartZ=0 EndX=2 EndY=-62 EndZ=0
    g12: LineSegment StartX=231.148 StartY=-12.5 StartZ=0 EndX=253 EndY=-12.5 EndZ=0
    g13: LineSegment StartX=253 StartY=-12.5 StartZ=0 EndX=253 EndY=0 EndZ=0
    g14: LineSegment StartX=253 StartY=0 StartZ=0 EndX=231.148 EndY=0 EndZ=0
    g15: LineSegment StartX=231.148 StartY=0 StartZ=0 EndX=231.148 EndY=-12.5 EndZ=0
    g16: LineSegment StartX=253 StartY=0 StartZ=0 EndX=253 EndY=-12.5 EndZ=0
    g17: LineSegment StartX=253 StartY=-12.5 StartZ=0 EndX=274.852 EndY=-12.5 EndZ=0
    g18: LineSegment StartX=274.852 StartY=-12.5 StartZ=0 EndX=274.852 EndY=0 EndZ=0
    g19: LineSegment StartX=274.852 StartY=0 StartZ=0 EndX=253 EndY=0 EndZ=0
    g20: LineSegment StartX=231.148 StartY=-62 StartZ=0 EndX=253 EndY=-62 EndZ=0
    g21: LineSegment StartX=253 StartY=-62 StartZ=0 EndX=253 EndY=-49.5 EndZ=0
    g22: LineSegment StartX=253 StartY=-49.5 StartZ=0 EndX=231.148 EndY=-49.5 EndZ=0
    g23: LineSegment StartX=231.148 StartY=-49.5 StartZ=0 EndX=231.148 EndY=-62 EndZ=0
    g24: LineSegment StartX=253 StartY=-49.5 StartZ=0 EndX=253 EndY=-62 EndZ=0
    g25: LineSegment StartX=253 StartY=-62 StartZ=0 EndX=274.852 EndY=-62 EndZ=0
    g26: LineSegment StartX=274.852 StartY=-62 StartZ=0 EndX=274.852 EndY=-49.5 EndZ=0
    g27: LineSegment StartX=274.852 StartY=-49.5 StartZ=0 EndX=253 EndY=-49.5 EndZ=0
    g28: LineSegment StartX=347 StartY=0 StartZ=0 EndX=334.5 EndY=0 EndZ=0
    g29: LineSegment StartX=334.5 StartY=0 StartZ=0 EndX=334.5 EndY=-21.8519 EndZ=0
    g30: LineSegment StartX=334.5 StartY=-21.8519 StartZ=0 EndX=347 EndY=-21.8519 EndZ=0
    g31: LineSegment StartX=347 StartY=-21.8519 StartZ=0 EndX=347 EndY=0 EndZ=0
    g32: LineSegment StartX=347 StartY=-62 StartZ=0 EndX=347 EndY=-40.1481 EndZ=0
    g33: LineSegment StartX=347 StartY=-40.1481 StartZ=0 EndX=334.5 EndY=-40.1481 EndZ=0
    g34: LineSegment StartX=334.5 StartY=-40.1481 StartZ=0 EndX=334.5 EndY=-62 EndZ=0
    g35: LineSegment StartX=334.5 StartY=-62 StartZ=0 EndX=347 EndY=-62 EndZ=0
  constraints (100):
    c: Coincident(g0,g1)
    c: Coincident(g1,g2)
    c: Coincident(g2,g3)
    c: Coincident(g3,g0)
    c: Vertical(g0)
    c: Vertical(g2)
    c: Horizontal(g1)
    c: Horizontal(g3)
    c: Coincident(g0,g-5)
    c: Coincident(g1,g-4)
    c: Coincident(g4,g5)
    c: Coincident(g5,g6)
    c: Coincident(g6,g7)
    c: Coincident(g7,g4)
    c: Vertical(g4)
    c: Vertical(g6)
    c: Horizontal(g5)
    c: Horizontal(g7)
    c: Coincident(g4,g0)
    c: Distance(g6) = 21.8519
    c: Distance(g5) = 12.5
    c: Coincident(g8,g9)
    c: Coincident(g9,g10)
    c: Coincident(g10,g11)
    c: Coincident(g11,g8)
    c: Horizontal(g8)
    c: Horizontal(g10)
    c: Vertical(g9)
    c: Vertical(g11)
    c: Coincident(g8,g0)
    c: Vertical(g9,g5)
    c: Equal(g9,g6)
    c: Coincident(g12,g13)
    c: Coincident(g13,g14)
    c: Coincident(g14,g15)
    c: Coincident(g15,g12)
    c: Horizontal(g12)
    c: Horizontal(g14)
    c: Vertical(g13)
    c: Vertical(g15)
    c: PointOnObject(g13,g3)
    c: Coincident(g16,g17)
    c: Coincident(g17,g18)
    c: Coincident(g18,g19)
    c: Coincident(g19,g16)
    c: Vertical(g16)
    c: Vertical(g18)
    c: Horizontal(g17)
    c: Horizontal(g19)
    c: Coincident(g16,g13)
    c: Equal(g15,g18)
    c: Equal(g18,g5)
    c: Equal(g17,g12)
    c: Equal(g12,g6)
    c: DistanceX(g-1,g13) = 253
    c: Coincident(g20,g21)
    c: Coincident(g21,g22)
    c: Coincident(g22,g23)
    c: Coincident(g23,g20)
    c: Horizontal(g20)
    c: Horizontal(g22)
    c: Vertical(g21)
    c: Vertical(g23)
    c: PointOnObject(g20,g1)
    c: Equal(g23,g15)
    c: Equal(g22,g12)
    c: Coincident(g24,g25)
    c: Coincident(g25,g26)
    c: Coincident(g26,g27)
    c: Coincident(g27,g24)
    c: Vertical(g24)
    c: Vertical(g26)
    c: Horizontal(g25)
    c: Horizontal(g27)
    c: Coincident(g24,g21)
    c: PointOnObject(g25,g1)
    c: Equal(g27,g17)
    c: Vertical(g21,g12)
    c: Coincident(g28,g29)
    c: Coincident(g29,g30)
    c: Coincident(g30,g31)
    c: Coincident(g31,g28)
    c: Horizontal(g28)
    c: Horizontal(g30)
    c: Vertical(g29)
    c: Vertical(g31)
    c: Coincident(g28,g2)
    c: Equal(g29,g17)
    c: Equal(g30,g18)
    c: Coincident(g32,g33)
    c: Coincident(g33,g34)
    c: Coincident(g34,g35)
    c: Coincident(g35,g32)
    c: Vertical(g32)
    c: Vertical(g34)
    c: Horizontal(g33)
    c: Horizontal(g35)
    c: Coincident(g32,g1)
    c: Vertical(g33,g29)
    c: Equal(g34,g29)
FEATURE [PartDesign::Body] Body  label="Housing"
  AllowCompound = false
  Configuration = 0
  Group = -> [Sketch,Sketch001,Pad,Pocket,DatumPlane,DatumPlane007,DatumPlane008,Sketch015,Sketch016,DatumPlane009,DatumPlane010,DatumLine,DatumPoint,DatumLine001,DatumPlane011,Sketch019,Sketch020,Groove,Revolution,Sketch021,Pocket010,Sketch024,Pocket013,LinearPattern,DatumPlane014,Sketch028,Sketch029,Binder001,Sketch031,Binder002,Sketch032,Pocket015,Sketch033,DatumPlane016,Sketch034]
  Origin = -> Origin
  Tip = -> Pocket015
  expr: .Configuration.Enum = Spreadsheet.cells[<<A3:|>>]
COMPONENT P6 — geometry summary ("LDR001"; no construction recipe available for this part):
  bounding box: 7.0 x 4.9 x 4.3 mm
  tessellated surface: 388 triangles
  volume: 39 mm^3 (26% of its bounding box)
  symmetry: 2-fold rotationally symmetric about the z axis
COMPONENT P7 — recipe-attached ("MountBracket003", a linked part whose construction recipe lives in a companion FreeCAD document of the same project; that document's serialized recipe follows).
Construction recipe (the companion document, serialized — sketch geometry with constraints, then the solid features built on it; lengths are millimeters unless a unit is written):

FCSTD DOCUMENT  (FreeCAD 1.0R39109 (Git))
Label: mount_bracket
License: All rights reserved
LicenseURL: https://en.wikipedia.org/wiki/All_rights_reserved
objects: Sketcher::SketchObject×3, PartDesign::Pocket×2, Spreadsheet::Sheet×1, PartDesign::Plane×1, PartDesign::Pad×1, PartDesign::Body×1
note: 17 computed .brp shape members not serialized (recipe doc carries the construction recipe); baked Part::Feature solids carry a one-line shape summary decoded from their .brp

FEATURE [Spreadsheet::Sheet] Spreadsheet  label="DisplaySS"
  Configuration = 1
  cells = A1='Variant; B1='threaded_insert_depth; C1='squared_profile_section_length; D1='threaded_insert_outer_diameter; E1='threaded_insert_safety_zone; F1='mount_bracket_face_size; G1='mount_bracket_length; H1='mount_bracket_draft_angle; I1='rear_countersink_offset; J1='rear_countersink_diameter; K1='rear_countersink_depth; A2==hiddenref(.Configuration.String); B2(threaded_insert_depth)==.B4; C2(squared_profile_section_length)==.C4; D2(threaded_insert_outer_diameter)==.D4; E2(threaded_insert_safety_zone)==.E4; F2(mount_bracket_face_size)==.F4; G2(mount_bracket_length)==.G4; H2(mount_bracket_draft_angle)==.H4; I2(rear_countersink_offset)==.I4; J2(rear_countersink_diameter)==.J4; K2(rear_countersink_depth)==.K4; A3='Female; B3==4 mm; C3==threaded_insert_depth; D3==5 mm; E3==2 mm; F3==12.5 mm; G3==mount_bracket_face_size / tan(mount_bracket_draft_angle) + threaded_insert_depth; H3==35 deg; I3==0 mm; J3==threaded_insert_outer_diameter; K3==threaded_insert_depth; A4='Male; B4==50 mm; C4==4 mm; D4==2 mm; E4==1 mm; F4==12.5 mm; G4==mount_bracket_face_size / tan(mount_bracket_draft_angle) + squared_profile_section_length; H4==35 deg; I4==squared_profile_section_length; J4==4 mm; K4==mount_bracket_length
  expr: .Configuration.Enum = cells[<<A3:|>>]
  expr: .cells.Bind.B2.ZZ2 = tuple(.cells; <<B>> + str(hiddenref(Configuration) + 3); <<ZZ>> + str(hiddenref(Configuration) + 3))
FEATURE [Sketcher::SketchObject] Sketch011  label="Threaded Barrel"
  ArcFitTolerance = 1e-06
  AttachmentSupport = -> [XZ_Plane003]
  FullyConstrained = true
  MakeInternals = false
  MapMode = 5
  Placement = pos=(0,0,0) rot=(1,0,0;1.5708rad)
  expr: Constraints[0] = <<DisplaySS>>.threaded_insert_outer_diameter
  expr: Constraints[1] = <<DisplaySS>>.mount_bracket_face_size / 2
  expr: Constraints[2] = <<DisplaySS>>.mount_bracket_face_size / 2
  sketch-geometry (1):
    g0: Circle CenterX=6.25 CenterY=6.25 CenterZ=0 NormalX=0 NormalY=0 NormalZ=1 AngleXU=0 Radius=1
  constraints (3):
    c: Diameter(g0) = 2
    c: DistanceY(g-1,g0) = 6.25
    c: DistanceX(g-2,g0) = 6.25
FEATURE [Sketcher::SketchObject] Sketch010
  ArcFitTolerance = 1e-06
  AttachmentSupport = -> [XY_Plane003]
  FullyConstrained = true
  MakeInternals = false
  MapMode = 4
  Placement = pos=(0,0,0) rot=(0.57735,0.57735,0.57735;2.0944rad)
  expr: Constraints[10] = <<DisplaySS>>.mount_bracket_face_size
  expr: Constraints[8] = <<DisplaySS>>.mount_bracket_draft_angle
  expr: Constraints[9] = <<DisplaySS>>.squared_profile_section_length
  sketch-geometry (4):
    g0: LineSegment StartX=-21.8519 StartY=-1.8e-15 StartZ=0 EndX=0 EndY=0 EndZ=0
    g1: LineSegment StartX=0 StartY=0 StartZ=0 EndX=0 EndY=12.5 EndZ=0
    g2: LineSegment StartX=0 StartY=12.5 StartZ=0 EndX=-4 EndY=12.5 EndZ=0
    g3: LineSegment StartX=-4 StartY=12.5 StartZ=0 EndX=-21.8519 EndY=-1.8e-15 EndZ=0
  constraints (11):
    c: PointOnObject(g0,g-1)
    c: Coincident(g0,g-1)
    c: Coincident(g0,g1)
    c: PointOnObject(g1,g-2)
    c: Coincident(g1,g2)
    c: Horizontal(g2)
    c: Coincident(g2,g3)
    c: Coincident(g3,g0)
    c: Angle(g0,g3) = 0.610865
    c: Distance(g2) = 4
    c: Distance(g1) = 12.5
FEATURE [PartDesign::Plane] DatumPlane  label="CountersinkPlane"
  AttachmentOffset = pos=(0,0,4) rot=(0,0,1;0rad)
  AttachmentSupport = -> [XZ_Plane003]
  Length = 60
  MapMode = 5
  Placement = pos=(0,-4,9e-16) rot=(1,0,0;1.5708rad)
  ResizeMode = 0
  Width = 60
  expr: .AttachmentOffset.Base.z = <<DisplaySS>>.rear_countersink_offset
FEATURE [Sketcher::SketchObject] Sketch  label="CountersinkSketch"
  ArcFitTolerance = 1e-06
  AttachmentSupport = -> [DatumPlane]
  ExternalGeometry = -> [Sketch011]
  FullyConstrained = true
  MakeInternals = false
  MapMode = 5
  Placement = pos=(0,-4,9e-16) rot=(1,0,0;1.5708rad)
  expr: Constraints[1] = <<DisplaySS>>.rear_countersink_diameter
  sketch-geometry (1):
    g0: Circle CenterX=6.25 CenterY=6.25 CenterZ=0 NormalX=0 NormalY=0 NormalZ=1 AngleXU=0 Radius=2
  constraints (2):
    c: Coincident(g0,g-3)
    c: Diameter(g0) = 4
FEATURE [PartDesign::Pad] Pad006
  Direction = (1,0,0)
  Length = 12.5
  Length2 = 10
  Profile = -> Sketch010
  ReferenceAxis = -> Sketch010 [N_Axis]
  Refine = true
  Suppressed = false
  Type = 0
  expr: Length = <<DisplaySS>>.mount_bracket_face_size
FEATURE [PartDesign::Pocket] Pocket015
  BaseFeature = -> Pad006
  Direction = (0,1,-2e-16)
  Length = 50
  Length2 = 5
  Profile = -> Sketch011
  ReferenceAxis = -> Sketch011 [N_Axis]
  Refine = true
  Reversed = true
  Suppressed = false
  Type = 0
  expr: Length = <<DisplaySS>>.threaded_insert_depth
FEATURE [PartDesign::Pocket] Pocket
  BaseFeature = -> Pocket015
  Direction = (0,1,-2e-16)
  Length = 21.8519
  Length2 = 5
  Profile = -> Sketch
  ReferenceAxis = -> Sketch [N_Axis]
  Refine = true
  Reversed = true
  Suppressed = false
  Type = 0
  expr: Length = <<DisplaySS>>.rear_countersink_depth
FEATURE [PartDesign::Body] Body003  label="MountBracket"
  AllowCompound = false
  Group = -> [Sketch010,Pad006,Sketch011,Pocket015,Sketch,Pocket,DatumPlane]
  Origin = -> Origin003
  Tip = -> Pocket
COMPONENT P8 — same part as P7; its construction recipe is shown at P7.
COMPONENT P9 — same part as P7; its construction recipe is shown at P7.
COMPONENT P10 — same part as P7; its construction recipe is shown at P7.
COMPONENT P11 — same part as P7; its construction recipe is shown at P7.
COMPONENT P12 — same part as P7; its construction recipe is shown at P7.
COMPONENT P13 — same part as P7; its construction recipe is shown at P7.
COMPONENT P14 — same part as P7; its construction recipe is shown at P7.
COMPONENT P15 — same part as P7; its construction recipe is shown at P7.
COMPONENT P16 — same part as P7; its construction recipe is shown at P7.
COMPONENT P17 — same part as P7; its construction recipe is shown at P7.
COMPONENT P18 — same part as P5; its construction recipe is shown at P5.
COMPONENT P19 — same part as P5; its construction recipe is shown at P5.
COMPONENT P20 — same part as P5; its construction recipe is shown at P5.
COMPONENT P21 — same part as P5; its construction recipe is shown at P5.
COMPONENT P22 — same part as P5; its construction recipe is shown at P5.
COMPONENT P23 — same part as P5; its construction recipe is shown at P5.
COMPONENT P24 — same part as P5; its construction recipe is shown at P5.
COMPONENT P25 — same part as P5; its construction recipe is shown at P5.
COMPONENT P26 — same part as P5; its construction recipe is shown at P5.
COMPONENT P27 — recipe-attached ("Mounting Plate001", modeled in this document).
Construction recipe (the document's own serialized feature program — sketch geometry with constraints, then the solid features built on it; lengths are millimeters unless a unit is written):

FEATURE [Sketcher::SketchObject] Sketch006  label="MountingPlateSketch"
  ArcFitTolerance = 1e-06
  AttachmentSupport = -> [XZ_Plane002]
  FullyConstrained = true
  MakeInternals = false
  MapMode = 5
  Placement = pos=(0,0,0) rot=(1,0,0;1.5708rad)
  expr: Constraints[10] = <<CalculatedSS>>.case_clear_opening_height
  expr: Constraints[9] = <<CalculatedSS>>.case_clear_opening_width
  sketch-geometry (4):
    g0: LineSegment StartX=0 StartY=0 StartZ=0 EndX=345 EndY=0 EndZ=0
    g1: LineSegment StartX=345 StartY=0 StartZ=0 EndX=345 EndY=94 EndZ=0
    g2: LineSegment StartX=345 StartY=94 StartZ=0 EndX=0 EndY=94 EndZ=0
    g3: LineSegment StartX=0 StartY=94 StartZ=0 EndX=0 EndY=0 EndZ=0
  constraints (11):
    c: Coincident(g0,g1)
    c: Coincident(g1,g2)
    c: Coincident(g2,g3)
    c: Coincident(g3,g0)
    c: Horizontal(g0)
    c: Horizontal(g2)
    c: Vertical(g1)
    c: Vertical(g3)
    c: Coincident(g0,g-1)
    c: Distance(g0) = 345
    c: Distance(g3) = 94
FEATURE [PartDesign::Pad] Pad002  label="MountingPlatePad"
  Direction = (0,-1,2e-16)
  Length = 5
  Length2 = 10
  Placement = pos=(0,0,0) rot=(1,0,0;1.5708rad)
  Profile = -> Sketch006
  ReferenceAxis = -> Sketch006 [N_Axis]
  Refine = true
  Suppressed = false
  Type = 0
  expr: Length = <<CalculatedSS>>.mounting_plate_thickness
FEATURE [Sketcher::SketchObject] Sketch007  label="Mounting Plate Screw Hole"
  ArcFitTolerance = 1e-06
  AttachmentSupport = -> [XZ_Plane002]
  FullyConstrained = true
  MakeInternals = false
  MapMode = 5
  Placement = pos=(0,0,0) rot=(1,0,0;1.5708rad)
  expr: Constraints[0] = <<DisplaySS>>.screw_diameter
  expr: Constraints[1] = <<CalculatedSS>>.screw_horizontal_offset
  expr: Constraints[2] = <<CalculatedSS>>.screw_vertical_offset
  sketch-geometry (1):
    g0: Circle CenterX=6.25 CenterY=6.25 CenterZ=0 NormalX=0 NormalY=0 NormalZ=1 AngleXU=0 Radius=1
  constraints (3):
    c: Diameter(g0) = 2
    c: DistanceX(g-2,g0) = 6.25
    c: DistanceY(g-1,g0) = 6.25
FEATURE [PartDesign::Pocket] Pocket004  label="MountingPlateScrewHolePocket"
  BaseFeature = -> Pad002
  Direction = (0,1,-2e-16)
  Length = 5
  Length2 = 5
  Placement = pos=(0,0,0) rot=(1,0,0;1.5708rad)
  Profile = -> Sketch007
  ReferenceAxis = -> Sketch007 [N_Axis]
  Refine = true
  Reversed = true
  Suppressed = false
  Type = 0
  expr: Length = <<CalculatedSS>>.mounting_plate_thickness
FEATURE [PartDesign::Plane] DatumPlane004  label="Mounting Case Horizontal Dividing Plane"
  AttachmentOffset = pos=(0,0,-47) rot=(0,0,1;0rad)
  AttachmentSupport = -> [XZ_Plane002]
  Length = 397.203
  MapMode = 3
  Placement = pos=(0,0,47) rot=(1,0,0;3.14159rad)
  ResizeMode = 0
  Width = 77.2029
  expr: .AttachmentOffset.Base.z = <<CalculatedSS>>.case_clear_opening_height / 2 * -1
FEATURE [PartDesign::Plane] DatumPlane005  label="MountingCaseVerticalDividingPlane"
  AttachmentOffset = pos=(0,0,172.5) rot=(0,0,1;0rad)
  AttachmentSupport = -> [YZ_Plane002]
  Length = 65.4272
  MapMode = 5
  Placement = pos=(172.5,0,0) rot=(0.57735,0.57735,0.57735;2.0944rad)
  ResizeMode = 0
  Width = 134.427
  expr: .AttachmentOffset.Base.z = <<CalculatedSS>>.case_clear_opening_width / 2
FEATURE [PartDesign::Mirrored] Mirrored004
  MirrorPlane = -> DatumPlane004
  Placement = pos=(0,0,0) rot=(1,0,0;1.5708rad)
  Refine = true
  Suppressed = false
  TransformMode = 0
FEATURE [PartDesign::Mirrored] Mirrored005
  MirrorPlane = -> DatumPlane005
  Placement = pos=(0,0,0) rot=(1,0,0;1.5708rad)
  Refine = true
  Suppressed = false
  TransformMode = 0
FEATURE [PartDesign::MultiTransform] MultiTransform003  label="MountingPlateScrewHoles"
  BaseFeature = -> Pocket004
  Originals = -> [Pocket004]
  Placement = pos=(0,0,0) rot=(1,0,0;1.5708rad)
  Refine = true
  Suppressed = false
  TransformMode = 0
  Transformations = -> [Mirrored004,Mirrored005]
FEATURE [PartDesign::Plane] DatumPlane006  label="MountingPlateFacePlane"
  AttachmentOffset = pos=(0,0,5) rot=(0,0,1;0rad)
  AttachmentSupport = -> [XZ_Plane002]
  Length = 411.967
  MapMode = 5
  Placement = pos=(0,-5,1.1e-15) rot=(1,0,0;1.5708rad)
  ResizeMode = 0
  Width = 160.967
  expr: .AttachmentOffset.Base.z = <<CalculatedSS>>.mounting_plate_thickness
FEATURE [Sketcher::SketchObject] Sketch008  label="LedPanelSketch"
  ArcFitTolerance = 1e-06
  AttachmentSupport = -> [DatumPlane006]
  FullyConstrained = true
  MakeInternals = false
  MapMode = 5
  Placement = pos=(0,-5,1.1e-15) rot=(1,0,0;1.5708rad)
  expr: Constraints[10] = <<CalculatedSS>>.case_clear_opening_height - <<CalculatedSS>>.grid_vertical_padding
  expr: Constraints[11] = <<CalculatedSS>>.case_clear_opening_width - <<CalculatedSS>>.grid_horizontal_padding
  expr: Constraints[8] = <<CalculatedSS>>.grid_vertical_padding
  expr: Constraints[9] = <<CalculatedSS>>.grid_horizontal_padding
  sketch-geometry (4):
    g0: LineSegment StartX=12.5 StartY=87 StartZ=0 EndX=12.5 EndY=7 EndZ=0
    g1: LineSegment StartX=12.5 StartY=7 StartZ=0 EndX=332.5 EndY=7 EndZ=0
    g2: LineSegment StartX=332.5 StartY=7 StartZ=0 EndX=332.5 EndY=87 EndZ=0
    g3: LineSegment StartX=332.5 StartY=87 StartZ=0 EndX=12.5 EndY=87 EndZ=0
  constraints (12):
    c: Coincident(g0,g1)
    c: Coincident(g1,g2)
    c: Coincident(g2,g3)
    c: Coincident(g3,g0)
    c: Vertical(g0)
    c: Vertical(g2)
    c: Horizontal(g1)
    c: Horizontal(g3)
    c: DistanceY(g-1,g0) = 7
    c: DistanceX(g-2,g0) = 12.5
    c: DistanceY(g-1,g0) = 87
    c: DistanceX(g-2,g1) = 332.5
FEATURE [PartDesign::Pocket] Pocket005  label="LEDMatrixPocket"
  BaseFeature = -> MultiTransform003
  Direction = (0,1,-2e-16)
  Length = 2
  Length2 = 5
  Placement = pos=(0,0,0) rot=(1,0,0;1.5708rad)
  Profile = -> Sketch008
  ReferenceAxis = -> Sketch008 [N_Axis]
  Refine = true
  Suppressed = false
  Type = 0
  expr: Length = <<DisplaySS>>.matrix_depth
FEATURE [Sketcher::SketchObject] Sketch009  label="MountPanelPassThroughSketch"
  ArcFitTolerance = 1e-06
  AttachmentSupport = -> [DatumPlane006]
  FullyConstrained = true
  MakeInternals = false
  MapMode = 5
  Placement = pos=(0,-5,1.1e-15) rot=(1,0,0;1.5708rad)
  expr: Constraints[10] = <<DisplaySS>>.matrix_width - <<DisplaySS>>.mount_panel_exclusion_offset * 2
  expr: Constraints[11] = <<DisplaySS>>.mount_panel_exclusion_offset + <<CalculatedSS>>.grid_horizontal_padding
  expr: Constraints[8] = <<CalculatedSS>>.grid_vertical_padding + <<DisplaySS>>.mount_panel_exclusion_offset
  expr: Constraints[9] = <<CalculatedSS>>.case_clear_opening_height - <<CalculatedSS>>.grid_vertical_padding - <<DisplaySS>>.mount_panel_exclusion_offset
  sketch-geometry (4):
    g0: LineSegment StartX=32.5 StartY=67 StartZ=0 EndX=32.5 EndY=27 EndZ=0
    g1: LineSegment StartX=32.5 StartY=27 StartZ=0 EndX=312.5 EndY=27 EndZ=0
    g2: LineSegment StartX=312.5 StartY=27 StartZ=0 EndX=312.5 EndY=67 EndZ=0
    g3: LineSegment StartX=312.5 StartY=67 StartZ=0 EndX=32.5 EndY=67 EndZ=0
  constraints (12):
    c: Coincident(g0,g1)
    c: Coincident(g1,g2)
    c: Coincident(g2,g3)
    c: Coincident(g3,g0)
    c: Vertical(g0)
    c: Vertical(g2)
    c: Horizontal(g1)
    c: Horizontal(g3)
    c: DistanceY(g-1,g0) = 27
    c: DistanceY(g-1,g0) = 67
    c: Distance(g3) = 280
    c: DistanceX(g-2,g0) = 32.5
FEATURE [PartDesign::Pocket] Pocket006  label="MountPanelPassThrough"
  BaseFeature = -> Pocket005
  Direction = (0,1,-2e-16)
  Length = 5
  Length2 = 5
  Placement = pos=(0,0,0) rot=(1,0,0;1.5708rad)
  Profile = -> Sketch009
  ReferenceAxis = -> Sketch009 [N_Axis]
  Refine = true
  Suppressed = false
  Type = 1
FEATURE [PartDesign::Body] Body002  label="Mounting Plate"
  AllowCompound = false
  Group = -> [Sketch006,Pad002,Sketch007,Pocket004,DatumPlane004,DatumPlane005,MultiTransform003,Mirrored004,Mirrored005,DatumPlane006,Sketch008,Pocket005,Sketch009,Pocket006]
  Origin = -> Origin002
  Tip = -> Pocket006
COMPONENT P28 — recipe-attached ("Protoboard Body", a linked part whose construction recipe lives in a companion FreeCAD document of the same project; that document's serialized recipe follows).
Construction recipe (the companion document, serialized — sketch geometry with constraints, then the solid features built on it; lengths are millimeters unless a unit is written):

FCSTD DOCUMENT  (FreeCAD 1.0R39109 (Git))
Label: Protoboard
License: All rights reserved
LicenseURL: https://en.wikipedia.org/wiki/All_rights_reserved
objects: Spreadsheet::Sheet×1, Sketcher::SketchObject×1, PartDesign::Pad×1, PartDesign::Body×1
note: 6 computed .brp shape members not serialized (recipe doc carries the construction recipe); baked Part::Feature solids carry a one-line shape summary decoded from their .brp

FEATURE [Spreadsheet::Sheet] Spreadsheet004  label="ProtoboardSS"
  cells = A1='Total Length; B1(total_length)==172.7 mm; A2='Mount Hole Spacing Length; B2(mount_spacing_length)==162.6 mm; A3='Mount Hole Spacing Width; B3(mount_spacing_width)==35.6 mm; A4='Total Width; B4(total_width)==52.1 mm; A5='Pins Width; B5(pin_width)==157.4 mm; A6='One Side Pin Margin; B6(pin_margin)==(total_length - pin_width) / 2; A7='Pitch; B7(pitch)==2.54 mm; A8='Mount to Pin Offset; B8(mount_pin_offset)==(mount_spacing_length - pin_width) / 2; A9='PCB Thickness; B9(thickness)==1.57 mm; A10='Mount Hole Side Offset; B10(mount_hole_side_offset)==(total_width - mount_spacing_width) / 2; A11='Mount Hole Top Offset; B11(mount_top_offset)==(total_length - mount_spacing_length) / 2; A12='M2 Mount Hole Size; B12(mount_hole_diameter)==2.2 mm; A13='first_pin_row_start; B13(first_pin_row_start)==(total_length - pin_width) / 2
FEATURE [Sketcher::SketchObject] Sketch020
  ArcFitTolerance = 1e-06
  AttachmentSupport = -> [XZ_Plane009]
  FullyConstrained = true
  MakeInternals = false
  MapMode = 5
  Placement = pos=(0,0,0) rot=(1,0,0;1.5708rad)
  expr: Constraints[10] = <<ProtoboardSS>>.total_length
  expr: Constraints[14] = <<ProtoboardSS>>.mount_hole_diameter
  expr: Constraints[15] = <<ProtoboardSS>>.mount_top_offset
  expr: Constraints[16] = <<ProtoboardSS>>.mount_hole_side_offset
  expr: Constraints[17] = <<ProtoboardSS>>.mount_top_offset
  expr: Constraints[18] = <<ProtoboardSS>>.total_width - <<ProtoboardSS>>.mount_hole_side_offset
  expr: Constraints[19] = <<ProtoboardSS>>.mount_hole_side_offset
  expr: Constraints[20] = <<ProtoboardSS>>.mount_top_offset
  expr: Constraints[21] = <<ProtoboardSS>>.mount_hole_side_offset
  expr: Constraints[22] = <<ProtoboardSS>>.mount_top_offset
  expr: Constraints[9] = <<ProtoboardSS>>.total_width
  sketch-geometry (12):
    g0: LineSegment StartX=0 StartY=0 StartZ=0 EndX=52.1 EndY=0 EndZ=0
    g1: LineSegment StartX=52.1 StartY=0 StartZ=0 EndX=52.1 EndY=172.7 EndZ=0
    g2: LineSegment StartX=52.1 StartY=172.7 StartZ=0 EndX=0 EndY=172.7 EndZ=0
    g3: LineSegment StartX=0 StartY=172.7 StartZ=0 EndX=0 EndY=0 EndZ=0
    g4: Circle CenterX=8.25 CenterY=167.65 CenterZ=0 NormalX=0 NormalY=0 NormalZ=1 AngleXU=0 Radius=1.1
    g5: Circle CenterX=43.85 CenterY=167.65 CenterZ=0 NormalX=0 NormalY=0 NormalZ=1 AngleXU=0 Radius=1.1
    g6: Circle CenterX=43.85 CenterY=5.05 CenterZ=0 NormalX=0 NormalY=0 NormalZ=1 AngleXU=0 Radius=1.1
    g7: Circle CenterX=8.25 CenterY=5.05 CenterZ=0 NormalX=0 NormalY=0 NormalZ=1 AngleXU=0 Radius=1.1
    g8: GeomPoint X=8.25 Y=5.05 Z=0
    g9: GeomPoint X=43.85 Y=5.05 Z=0
    g10: GeomPoint X=43.85 Y=167.65 Z=0
    g11: GeomPoint X=8.25 Y=167.65 Z=0
  constraints (27):
    c: Coincident(g0,g1)
    c: Coincident(g1,g2)
    c: Coincident(g2,g3)
    c: Coincident(g3,g0)
    c: Horizontal(g0)
    c: Horizontal(g2)
    c: Vertical(g1)
    c: Vertical(g3)
    c: Coincident(g-1,g0)
    c: Distance(g0) = 52.1
    c: Distance(g3) = 172.7
    c: Equal(g7,g6)
    c: Equal(g7,g5)
    c: Equal(g7,g4)
    c: Diameter(g7) = 2.2
    c: Distance(g4,g2) = 5.05
    c: Distance(g4,g3) = 8.25
    c: Distance(g5,g2) = 5.05
    c: Distance(g5,g3) = 43.85
    c: Distance(g7,g3) = 8.25
    c: DistanceY(g-1,g7) = 5.05
    c: Distance(g6,g1) = 8.25
    c: Distance(g6,g0) = 5.05
    c: Coincident(g8,g7)
    c: Coincident(g9,g6)
    c: Coincident(g10,g5)
    c: Coincident(g11,g4)
FEATURE [PartDesign::Pad] Pad007  label="Protoboard Pad"
  Direction = (0,-1,2e-16)
  Length = 1.57
  Length2 = 10
  Placement = pos=(0,0,0) rot=(1,0,0;1.5708rad)
  Profile = -> Sketch020
  ReferenceAxis = -> Sketch020 [N_Axis]
  Refine = true
  Suppressed = false
  Type = 0
  expr: Length = <<ProtoboardSS>>.thickness
FEATURE [PartDesign::Body] Body007  label="Protoboard Body"
  AllowCompound = false
  Group = -> [Sketch020,Pad007]
  Origin = -> Origin009
  Tip = -> Pad007
COMPONENT P29 — recipe-attached ("Screen001", modeled in this document).
Construction recipe (the document's own serialized feature program — sketch geometry with constraints, then the solid features built on it; lengths are millimeters unless a unit is written):

FEATURE [Sketcher::SketchObject] Sketch012
  ArcFitTolerance = 1e-06
  AttachmentSupport = -> [XZ_Plane004]
  FullyConstrained = true
  MakeInternals = false
  MapMode = 5
  Placement = pos=(0,0,0) rot=(1,0,0;1.5708rad)
  expr: Constraints[10] = <<CalculatedSS>>.case_width
  expr: Constraints[9] = <<CalculatedSS>>.case_height
  sketch-geometry (4):
    g0: LineSegment StartX=0 StartY=0 StartZ=0 EndX=349 EndY=0 EndZ=0
    g1: LineSegment StartX=349 StartY=0 StartZ=0 EndX=349 EndY=98 EndZ=0
    g2: LineSegment StartX=349 StartY=98 StartZ=0 EndX=0 EndY=98 EndZ=0
    g3: LineSegment StartX=0 StartY=98 StartZ=0 EndX=0 EndY=0 EndZ=0
  constraints (11):
    c: Coincident(g0,g1)
    c: Coincident(g1,g2)
    c: Coincident(g2,g3)
    c: Coincident(g3,g0)
    c: Horizontal(g0)
    c: Horizontal(g2)
    c: Vertical(g1)
    c: Vertical(g3)
    c: Coincident(g0,g-1)
    c: Distance(g3) = 98
    c: Distance(g0) = 349
FEATURE [PartDesign::Pad] Pad004  label="Glass"
  Direction = (0,-1,2e-16)
  Length = 3
  Length2 = 10
  Placement = pos=(0,0,0) rot=(1,0,0;1.5708rad)
  Profile = -> Sketch012
  ReferenceAxis = -> Sketch012 [N_Axis]
  Refine = true
  Suppressed = false
  Type = 0
  expr: Length = <<DisplaySS>>.glass_thickness
FEATURE [Sketcher::SketchObject] Sketch013  label="Magnet Placement"
  ArcFitTolerance = 1e-06
  AttachmentSupport = -> [XZ_Plane004]
  FullyConstrained = true
  MakeInternals = false
  MapMode = 5
  Placement = pos=(0,0,0) rot=(1,0,0;1.5708rad)
  expr: Constraints[0] = <<CalculatedSS>>.case_relative_magnet_vertical_offset
  expr: Constraints[10] = <<CalculatedSS>>.case_width - <<CalculatedSS>>.case_relative_magnet_horizontal_offset
  expr: Constraints[11] = <<CalculatedSS>>.case_relative_magnet_vertical_offset
  expr: Constraints[1] = <<CalculatedSS>>.case_relative_magnet_horizontal_offset
  expr: Constraints[2] = <<DisplaySS>>.magnet_diameter
  expr: Constraints[3] = <<DisplaySS>>.magnet_diameter
  expr: Constraints[4] = <<DisplaySS>>.magnet_diameter
  expr: Constraints[5] = <<DisplaySS>>.magnet_diameter
  expr: Constraints[6] = <<CalculatedSS>>.case_height - <<CalculatedSS>>.case_relative_magnet_vertical_offset
  expr: Constraints[7] = <<CalculatedSS>>.case_height - <<CalculatedSS>>.case_relative_magnet_vertical_offset
  expr: Constraints[8] = <<CalculatedSS>>.case_relative_magnet_horizontal_offset
  expr: Constraints[9] = <<CalculatedSS>>.case_width - <<CalculatedSS>>.case_relative_magnet_horizontal_offset
  sketch-geometry (4):
    g0: Circle CenterX=8.25 CenterY=20.8 CenterZ=0 NormalX=0 NormalY=0 NormalZ=1 AngleXU=0 Radius=2.5
    g1: Circle CenterX=8.25 CenterY=77.2 CenterZ=0 NormalX=0 NormalY=0 NormalZ=1 AngleXU=0 Radius=2.5
    g2: Circle CenterX=340.75 CenterY=77.2 CenterZ=0 NormalX=0 NormalY=0 NormalZ=1 AngleXU=0 Radius=2.5
    g3: Circle CenterX=340.75 CenterY=20.8 CenterZ=0 NormalX=0 NormalY=0 NormalZ=1 AngleXU=0 Radius=2.5
  constraints (12):
    c: DistanceY(g-1,g0) = 20.8
    c: DistanceX(g-2,g0) = 8.25
    c: Diameter(g0) = 5
    c: Diameter(g1) = 5
    c: Diameter(g2) = 5
    c: Diameter(g3) = 5
    c: DistanceY(g-1,g1) = 77.2
    c: DistanceY(g-1,g2) = 77.2
    c: DistanceX(g-2,g1) = 8.25
    c: DistanceX(g-2,g2) = 340.75
    c: DistanceX(g-2,g3) = 340.75
    c: DistanceY(g-1,g3) = 20.8
FEATURE [PartDesign::Body] Body004  label="Screen"
  AllowCompound = false
  Group = -> [Sketch012,Pad004,Sketch013]
  Origin = -> Origin004
  Tip = -> Pad004
COMPONENT P30 — same part as P5; its construction recipe is shown at P5.
COMPONENT P31 — same part as P5; its construction recipe is shown at P5.
PROVENANCE & LICENSES
A FreeCAD (.FCStd) document from a public repository crawl; recipes are the document's own serialized feature recipes (and, for linked parts, companion documents' recipes).
License: as declared in the source repository (recorded in the dataset sidecar).
